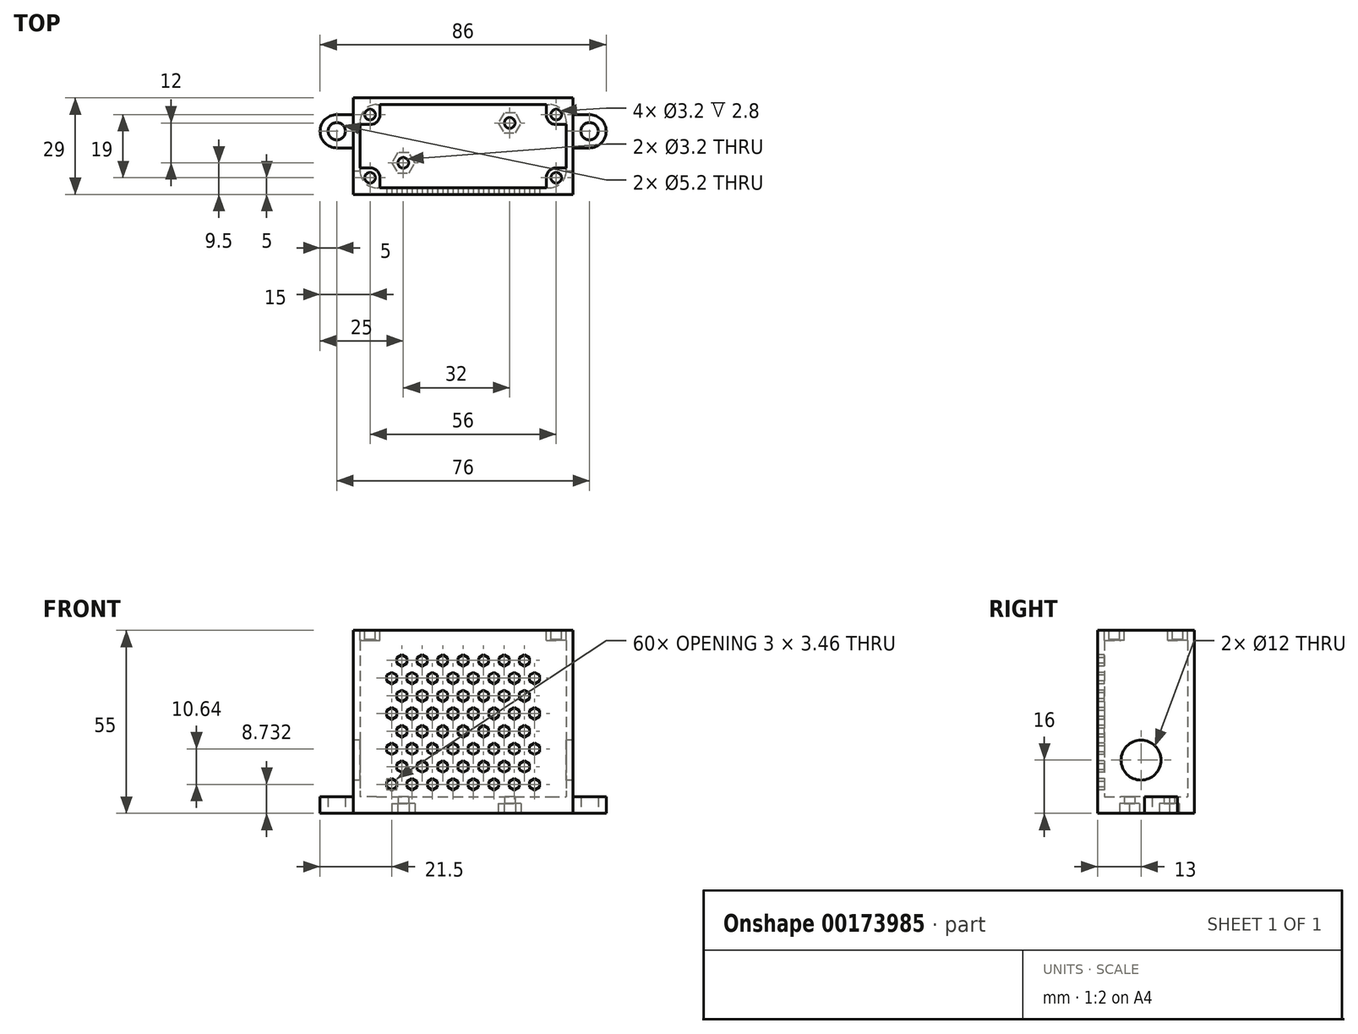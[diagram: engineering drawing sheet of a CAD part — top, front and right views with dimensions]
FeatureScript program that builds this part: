
annotation { "Feature Type Name" : "Feature", "Feature Type Description" : "" }
export const myFeature = defineFeature(function(context is Context, id is Id, definition is map)
    precondition{}
    {
        {
            var Q0;
            Q0=qCreatedBy(makeId("Top.planeOp"),FACE);
            var sketch = newSketch(context, id + "F0", { "sketchPlane" : qUnion([Q0])});
            skCircle(sketch, "E0", {"center": v(3, 5.5) * mm, "radius": 1.6 * mm});
            skCircle(sketch, "E1", {"center": v(35, 17.5) * mm, "radius": 1.6 * mm});
            skLineSegment(sketch, "E2.bottom", {"start": v(0, 0) * mm, "end": v(42, 0) * mm});
            skLineSegment(sketch, "E2.top", {"start": v(0, 21) * mm, "end": v(42, 21) * mm});
            skLineSegment(sketch, "E2.left", {"start": v(0, 0) * mm, "end": v(0, 21) * mm});
            skLineSegment(sketch, "E2.right", {"start": v(42, 0) * mm, "end": v(42, 21) * mm});
            skLineSegment(sketch, "E3.bottom", {"start": v(-12, 25) * mm, "end": v(54, 25) * mm});
            skLineSegment(sketch, "E3.top", {"start": v(-12, -4) * mm, "end": v(54, -4) * mm});
            skLineSegment(sketch, "E3.left", {"start": v(-12, 25) * mm, "end": v(-12, 20) * mm});
            skLineSegment(sketch, "E3.right", {"start": v(54, 25) * mm, "end": v(54, 20) * mm});
            skCircle(sketch, "E4", {"center": v(-17, 15) * mm, "radius": 2.6 * mm});
            skArc(sketch, "E5", {"start": v(-17, 20) * mm, "mid": v(-22, 15) * mm, "end": v(-17, 10) * mm});
            skCircle(sketch, "E6", {"center": v(59, 15) * mm, "radius": 2.6 * mm});
            skArc(sketch, "E7", {"start": v(59, 10) * mm, "mid": v(64, 15) * mm, "end": v(59, 20) * mm});
            skLineSegment(sketch, "E8", {"start": v(-17, 20) * mm, "end": v(-12, 20) * mm});
            skLineSegment(sketch, "E9", {"start": v(-17, 10) * mm, "end": v(-12, 10) * mm});
            skLineSegment(sketch, "E10", {"start": v(59, 20) * mm, "end": v(54, 20) * mm});
            skLineSegment(sketch, "E11", {"start": v(59, 10) * mm, "end": v(54, 10) * mm});
            skLineSegment(sketch, "E12.trimOffspring", {"start": v(54, 10) * mm, "end": v(54, -4) * mm});
            skLineSegment(sketch, "E13.trimOffspring", {"start": v(-12, 10) * mm, "end": v(-12, -4) * mm});
            skSolve(sketch);
        }
        {
            var Q0;
            Q0=makeQuery(id+"F0.imprint","IMPRINT",FACE,{"disambiguationData":[TD([[makeQuery(id+"F0.imprint","IMPRINT",EDGE,{"derivedFrom":sQuery(id+"F0.wireOp",EDGE,"E2.bottom")}),-1.0]])]});
            var Q1;
            Q1=makeQuery(id+"F0.imprint","IMPRINT",FACE,{"disambiguationData":[TD([[makeQuery(id+"F0.imprint","IMPRINT",EDGE,{"derivedFrom":sQuery(id+"F0.wireOp",EDGE,"E0")}),-1.0]])]});
            extrude(context, id + "F1", {"entities" : qUnion([Q0, Q1]), "depth" : 5 * mm});
        }
        {
            var Q0;
            Q0=makeQuery(id+"F1.opExtrude","CAP_FACE",FACE,{"disambiguationData":[OSD([sQuery(id+"F0.wireOp",EDGE,"E0"),sQuery(id+"F0.wireOp",EDGE,"E1"),sQuery(id+"F0.wireOp",EDGE,"E3.bottom"),sQuery(id+"F0.wireOp",EDGE,"E3.top"),sQuery(id+"F0.wireOp",EDGE,"E3.left"),sQuery(id+"F0.wireOp",EDGE,"E3.right"),sQuery(id+"F0.wireOp",EDGE,"E4"),sQuery(id+"F0.wireOp",EDGE,"E5"),sQuery(id+"F0.wireOp",EDGE,"E6"),sQuery(id+"F0.wireOp",EDGE,"E7"),sQuery(id+"F0.wireOp",EDGE,"E8"),sQuery(id+"F0.wireOp",EDGE,"E9"),sQuery(id+"F0.wireOp",EDGE,"E10"),sQuery(id+"F0.wireOp",EDGE,"E11"),sQuery(id+"F0.wireOp",EDGE,"E12.trimOffspring"),sQuery(id+"F0.wireOp",EDGE,"E13.trimOffspring")])],"isStart":false});
            var sketch = newSketch(context, id + "F2", { "sketchPlane" : qUnion([Q0])});
            skLineSegment(sketch, "E14.bottom", {"start": v(-10, 23) * mm, "end": v(52, 23) * mm});
            skLineSegment(sketch, "E14.top", {"start": v(-10, -2) * mm, "end": v(52, -2) * mm});
            skLineSegment(sketch, "E14.left", {"start": v(-10, 23) * mm, "end": v(-10, -2) * mm});
            skLineSegment(sketch, "E14.right", {"start": v(52, 23) * mm, "end": v(52, -2) * mm});
            skLineSegment(sketch, "E15.bottom", {"start": v(-12, 25) * mm, "end": v(54, 25) * mm});
            skLineSegment(sketch, "E15.top", {"start": v(-12, -4) * mm, "end": v(54, -4) * mm});
            skLineSegment(sketch, "E15.left", {"start": v(-12, 25) * mm, "end": v(-12, -4) * mm});
            skLineSegment(sketch, "E15.right", {"start": v(54, 25) * mm, "end": v(54, -4) * mm});
            skSolve(sketch);
        }
        {
            var Q0;
            Q0=makeQuery(id+"F2.imprint","IMPRINT",FACE,{"disambiguationData":[TD([[makeQuery(id+"F2.imprint","IMPRINT",EDGE,{"derivedFrom":sQuery(id+"F2.wireOp",EDGE,"E14.bottom")}),1.0]])]});
            extrude(context, id + "F3", {"entities" : qUnion([Q0]), "operationType" : NewBodyOperationType.ADD, "depth" : 50 * mm});
        }
        {
            var Q0;
            Q0=makeQuery(id+"F1.opExtrude","CAP_FACE",FACE,{"disambiguationData":[OSD([sQuery(id+"F0.wireOp",EDGE,"E0"),sQuery(id+"F0.wireOp",EDGE,"E1"),sQuery(id+"F0.wireOp",EDGE,"E3.bottom"),sQuery(id+"F0.wireOp",EDGE,"E3.top"),sQuery(id+"F0.wireOp",EDGE,"E3.left"),sQuery(id+"F0.wireOp",EDGE,"E3.right"),sQuery(id+"F0.wireOp",EDGE,"E4"),sQuery(id+"F0.wireOp",EDGE,"E5"),sQuery(id+"F0.wireOp",EDGE,"E6"),sQuery(id+"F0.wireOp",EDGE,"E7"),sQuery(id+"F0.wireOp",EDGE,"E8"),sQuery(id+"F0.wireOp",EDGE,"E9"),sQuery(id+"F0.wireOp",EDGE,"E10"),sQuery(id+"F0.wireOp",EDGE,"E11"),sQuery(id+"F0.wireOp",EDGE,"E12.trimOffspring"),sQuery(id+"F0.wireOp",EDGE,"E13.trimOffspring")])],"isStart":true});
            var sketch = newSketch(context, id + "F4", { "sketchPlane" : qUnion([Q0])});
            skCircle(sketch, "E16.cCircle", {"center": v(3, -5.5) * mm, "radius": 3 * mm, "construction": true});
            skLineSegment(sketch, "E16.0", {"start": v(1.27, -2.5) * mm, "end": v(4.73, -2.5) * mm});
            skLineSegment(sketch, "E16.1", {"start": v(4.73, -2.5) * mm, "end": v(6.46, -5.5) * mm});
            skLineSegment(sketch, "E16.2", {"start": v(6.46, -5.5) * mm, "end": v(4.73, -8.5) * mm});
            skLineSegment(sketch, "E16.3", {"start": v(4.73, -8.5) * mm, "end": v(1.27, -8.5) * mm});
            skLineSegment(sketch, "E16.4", {"start": v(1.27, -8.5) * mm, "end": v(-0.46, -5.5) * mm});
            skLineSegment(sketch, "E16.5", {"start": v(-0.46, -5.5) * mm, "end": v(1.27, -2.5) * mm});
            skPoint(sketch, "E16.0.midPoint", {"position": v(3, -2.5) * mm});
            skCircle(sketch, "E17.cCircle", {"center": v(35, -17.5) * mm, "radius": 3 * mm, "construction": true});
            skLineSegment(sketch, "E17.0", {"start": v(33.27, -14.5) * mm, "end": v(36.73, -14.5) * mm});
            skLineSegment(sketch, "E17.1", {"start": v(36.73, -14.5) * mm, "end": v(38.46, -17.5) * mm});
            skLineSegment(sketch, "E17.2", {"start": v(38.46, -17.5) * mm, "end": v(36.73, -20.5) * mm});
            skLineSegment(sketch, "E17.3", {"start": v(36.73, -20.5) * mm, "end": v(33.27, -20.5) * mm});
            skLineSegment(sketch, "E17.4", {"start": v(33.27, -20.5) * mm, "end": v(31.54, -17.5) * mm});
            skLineSegment(sketch, "E17.5", {"start": v(31.54, -17.5) * mm, "end": v(33.27, -14.5) * mm});
            skPoint(sketch, "E17.0.midPoint", {"position": v(35, -14.5) * mm});
            skSolve(sketch);
        }
        {
            var Q0;
            Q0=makeQuery(id+"F4.imprint","IMPRINT",FACE,{"disambiguationData":[TD([[makeQuery(id+"F4.imprint","IMPRINT",EDGE,{"derivedFrom":sQuery(id+"F4.wireOp",EDGE,"E16.0")}),-1.0]])]});
            var Q1;
            Q1=makeQuery(id+"F4.imprint","IMPRINT",FACE,{"disambiguationData":[TD([[makeQuery(id+"F4.imprint","IMPRINT",EDGE,{"derivedFrom":sQuery(id+"F4.wireOp",EDGE,"E17.0")}),-1.0]])]});
            extrude(context, id + "F5", {"entities" : qUnion([Q0, Q1]), "operationType" : NewBodyOperationType.REMOVE, "oppositeDirection" : true, "depth" : 3 * mm});
        }
        {
            var Q0;
            Q0=makeQuery(id+"F3.opExtrude","CAP_FACE",FACE,{"disambiguationData":[OSD([sQuery(id+"F2.wireOp",EDGE,"E14.bottom"),sQuery(id+"F2.wireOp",EDGE,"E14.top"),sQuery(id+"F2.wireOp",EDGE,"E14.left"),sQuery(id+"F2.wireOp",EDGE,"E14.right"),sQuery(id+"F2.wireOp",EDGE,"E15.bottom"),sQuery(id+"F2.wireOp",EDGE,"E15.top"),sQuery(id+"F2.wireOp",EDGE,"E15.left"),sQuery(id+"F2.wireOp",EDGE,"E15.right")])],"isStart":false});
            var sketch = newSketch(context, id + "F6", { "sketchPlane" : qUnion([Q0])});
            skArc(sketch, "E18", {"start": v(-7, 17) * mm, "mid": v(-4.88, 17.88) * mm, "end": v(-4, 20) * mm});
            skArc(sketch, "E19", {"start": v(46, 20) * mm, "mid": v(46.88, 17.88) * mm, "end": v(49, 17) * mm});
            skArc(sketch, "E20", {"start": v(49, 4) * mm, "mid": v(46.88, 3.12) * mm, "end": v(46, 1) * mm});
            skArc(sketch, "E21", {"start": v(-4, 1) * mm, "mid": v(-4.88, 3.12) * mm, "end": v(-7, 4) * mm});
            skLineSegment(sketch, "E22", {"start": v(-10, 23) * mm, "end": v(-10, 20) * mm});
            skLineSegment(sketch, "E23", {"start": v(-10, 23) * mm, "end": v(-7, 23) * mm});
            skLineSegment(sketch, "E24", {"start": v(-10, -2) * mm, "end": v(-10, 1) * mm});
            skLineSegment(sketch, "E25", {"start": v(-7, -2) * mm, "end": v(-10, -2) * mm});
            skLineSegment(sketch, "E26", {"start": v(52, -2) * mm, "end": v(49, -2) * mm});
            skLineSegment(sketch, "E27", {"start": v(52, -2) * mm, "end": v(52, 1) * mm});
            skLineSegment(sketch, "E28", {"start": v(52, 23) * mm, "end": v(49, 23) * mm});
            skLineSegment(sketch, "E29", {"start": v(52, 23) * mm, "end": v(52, 20) * mm});
            skLineSegment(sketch, "E30", {"start": v(46, 23) * mm, "end": v(46, 20) * mm});
            skLineSegment(sketch, "E31", {"start": v(52, 17) * mm, "end": v(49, 17) * mm});
            skLineSegment(sketch, "E32", {"start": v(52, 4) * mm, "end": v(49, 4) * mm});
            skLineSegment(sketch, "E33", {"start": v(46, -2) * mm, "end": v(46, 1) * mm});
            skLineSegment(sketch, "E34", {"start": v(-4, -2) * mm, "end": v(-4, 1) * mm});
            skLineSegment(sketch, "E35", {"start": v(-10, 4) * mm, "end": v(-7, 4) * mm});
            skLineSegment(sketch, "E36", {"start": v(-10, 17) * mm, "end": v(-7, 17) * mm});
            skLineSegment(sketch, "E37", {"start": v(-4, 23) * mm, "end": v(-4, 20) * mm});
            skSolve(sketch);
        }
        {
            var Q0;
            Q0=makeQuery(id+"F6.imprint","IMPRINT",FACE,{"disambiguationData":[TD([[makeQuery(id+"F6.imprint","IMPRINT",EDGE,{"derivedFrom":sQuery(id+"F6.wireOp",EDGE,"E19")}),1.0]])]});
            var Q1;
            Q1=makeQuery(id+"F6.imprint","IMPRINT",FACE,{"disambiguationData":[TD([[makeQuery(id+"F6.imprint","IMPRINT",EDGE,{"derivedFrom":sQuery(id+"F6.wireOp",EDGE,"E20")}),1.0]])]});
            var Q2;
            Q2=makeQuery(id+"F6.imprint","IMPRINT",FACE,{"disambiguationData":[TD([[makeQuery(id+"F6.imprint","IMPRINT",EDGE,{"derivedFrom":sQuery(id+"F6.wireOp",EDGE,"E21")}),1.0]])]});
            var Q3;
            Q3=makeQuery(id+"F6.imprint","IMPRINT",FACE,{"disambiguationData":[TD([[makeQuery(id+"F6.imprint","IMPRINT",EDGE,{"derivedFrom":sQuery(id+"F6.wireOp",EDGE,"E18")}),1.0]])]});
            extrude(context, id + "F7", {"entities" : qUnion([Q0, Q1, Q2, Q3]), "operationType" : NewBodyOperationType.ADD, "oppositeDirection" : true, "depth" : 3 * mm});
        }
        {
            var Q0;
            Q0=makeQuery(id+"F7.opExtrude","CAP_EDGE",EDGE,{"disambiguationData":[OSD([sQuery(id+"F2.wireOp",EDGE,"E14.top"),sQuery(id+"F6.wireOp",EDGE,"E25")])],"isStart":false});
            var Q1;
            Q1=makeQuery(id+"F7.opExtrude","CAP_EDGE",EDGE,{"disambiguationData":[OSD([sQuery(id+"F2.wireOp",EDGE,"E14.left"),sQuery(id+"F6.wireOp",EDGE,"E24")])],"isStart":false});
            var Q2;
            Q2=makeQuery(id+"F3.opExtrude","SWEPT_EDGE",EDGE,{"disambiguationData":[OSD([sQuery(id+"F2.wireOp",EDGE,"E14.top"),sQuery(id+"F2.wireOp",EDGE,"E14.left")])]});
            var Q3;
            Q3=makeQuery(id+"F3.opExtrude","SWEPT_EDGE",EDGE,{"disambiguationData":[OSD([sQuery(id+"F2.wireOp",EDGE,"E14.bottom"),sQuery(id+"F2.wireOp",EDGE,"E14.left")])]});
            var Q4;
            Q4=makeQuery(id+"F3.opExtrude","SWEPT_EDGE",EDGE,{"disambiguationData":[OSD([sQuery(id+"F2.wireOp",EDGE,"E14.bottom"),sQuery(id+"F2.wireOp",EDGE,"E14.right")])]});
            var Q5;
            Q5=makeQuery(id+"F3.opExtrude","SWEPT_EDGE",EDGE,{"disambiguationData":[OSD([sQuery(id+"F2.wireOp",EDGE,"E14.top"),sQuery(id+"F2.wireOp",EDGE,"E14.right")])]});
            var Q6;
            Q6=makeQuery(id+"F7.opExtrude","CAP_EDGE",EDGE,{"disambiguationData":[OSD([sQuery(id+"F2.wireOp",EDGE,"E14.left"),sQuery(id+"F6.wireOp",EDGE,"E22")])],"isStart":false});
            var Q7;
            Q7=makeQuery(id+"F7.opExtrude","CAP_EDGE",EDGE,{"disambiguationData":[OSD([sQuery(id+"F2.wireOp",EDGE,"E14.bottom"),sQuery(id+"F6.wireOp",EDGE,"E23")])],"isStart":false});
            var Q8;
            Q8=makeQuery(id+"F7.opExtrude","CAP_EDGE",EDGE,{"disambiguationData":[OSD([sQuery(id+"F2.wireOp",EDGE,"E14.right"),sQuery(id+"F6.wireOp",EDGE,"E29")])],"isStart":false});
            var Q9;
            Q9=makeQuery(id+"F7.opExtrude","CAP_EDGE",EDGE,{"disambiguationData":[OSD([sQuery(id+"F2.wireOp",EDGE,"E14.bottom"),sQuery(id+"F6.wireOp",EDGE,"E28")])],"isStart":false});
            var Q10;
            Q10=makeQuery(id+"F7.opExtrude","CAP_EDGE",EDGE,{"disambiguationData":[OSD([sQuery(id+"F2.wireOp",EDGE,"E14.top"),sQuery(id+"F6.wireOp",EDGE,"E26")])],"isStart":false});
            var Q11;
            Q11=makeQuery(id+"F7.opExtrude","CAP_EDGE",EDGE,{"disambiguationData":[OSD([sQuery(id+"F2.wireOp",EDGE,"E14.right"),sQuery(id+"F6.wireOp",EDGE,"E27")])],"isStart":false});
            fillet(context, id + "F8", {"entities" : qUnion([Q0, Q1, Q2, Q3, Q4, Q5, Q6, Q7, Q8, Q9, Q10, Q11]), "radius" : 5 * mm, "tangentPropagation" : true, "allowEdgeOverflow" : false});
        }
        {
            var Q0;
            {var subQ0=sQuery(id+"F2.wireOp",EDGE,"E14.left");var subQ1=sQuery(id+"F2.wireOp",EDGE,"E14.top");var subQ2=sQuery(id+"F2.wireOp",EDGE,"E14.right");var subQ3=sQuery(id+"F2.wireOp",EDGE,"E14.bottom");Q0=makeQuery(id+"F7.boolean.opBoolean","MERGE",FACE,{"derivedFrom":[makeQuery(id+"F3.opExtrude","CAP_FACE",FACE,{"disambiguationData":[OSD([subQ3,subQ1,subQ0,subQ2,sQuery(id+"F2.wireOp",EDGE,"E15.bottom"),sQuery(id+"F2.wireOp",EDGE,"E15.top"),sQuery(id+"F2.wireOp",EDGE,"E15.left"),sQuery(id+"F2.wireOp",EDGE,"E15.right")])],"isStart":false}),makeQuery(id+"F7.opExtrude","CAP_FACE",FACE,{"disambiguationData":[OSD([subQ3,subQ0,sQuery(id+"F6.wireOp",EDGE,"E18"),sQuery(id+"F6.wireOp",EDGE,"E22"),sQuery(id+"F6.wireOp",EDGE,"E23"),sQuery(id+"F6.wireOp",EDGE,"E36"),sQuery(id+"F6.wireOp",EDGE,"E37")])],"isStart":true}),makeQuery(id+"F7.opExtrude","CAP_FACE",FACE,{"disambiguationData":[OSD([subQ3,subQ2,sQuery(id+"F6.wireOp",EDGE,"E19"),sQuery(id+"F6.wireOp",EDGE,"E28"),sQuery(id+"F6.wireOp",EDGE,"E29"),sQuery(id+"F6.wireOp",EDGE,"E30"),sQuery(id+"F6.wireOp",EDGE,"E31")])],"isStart":true}),makeQuery(id+"F7.opExtrude","CAP_FACE",FACE,{"disambiguationData":[OSD([subQ1,subQ2,sQuery(id+"F6.wireOp",EDGE,"E20"),sQuery(id+"F6.wireOp",EDGE,"E26"),sQuery(id+"F6.wireOp",EDGE,"E27"),sQuery(id+"F6.wireOp",EDGE,"E32"),sQuery(id+"F6.wireOp",EDGE,"E33")])],"isStart":true}),makeQuery(id+"F7.opExtrude","CAP_FACE",FACE,{"disambiguationData":[OSD([subQ1,subQ0,sQuery(id+"F6.wireOp",EDGE,"E21"),sQuery(id+"F6.wireOp",EDGE,"E24"),sQuery(id+"F6.wireOp",EDGE,"E25"),sQuery(id+"F6.wireOp",EDGE,"E34"),sQuery(id+"F6.wireOp",EDGE,"E35")])],"isStart":true})]});}
            var sketch = newSketch(context, id + "F9", { "sketchPlane" : qUnion([Q0])});
            skCircle(sketch, "E38", {"center": v(-7, 20) * mm, "radius": 1.6 * mm});
            skCircle(sketch, "E39", {"center": v(-7, 1) * mm, "radius": 1.6 * mm});
            skCircle(sketch, "E40", {"center": v(49, 1) * mm, "radius": 1.6 * mm});
            skCircle(sketch, "E41", {"center": v(49, 20) * mm, "radius": 1.6 * mm});
            skSolve(sketch);
        }
        {
            var Q0;
            Q0=makeQuery(id+"F9.imprint","IMPRINT",FACE,{"disambiguationData":[TD([[makeQuery(id+"F9.imprint","IMPRINT",EDGE,{"derivedFrom":sQuery(id+"F9.wireOp",EDGE,"E38")}),1.0]])]});
            var Q1;
            Q1=makeQuery(id+"F9.imprint","IMPRINT",FACE,{"disambiguationData":[TD([[makeQuery(id+"F9.imprint","IMPRINT",EDGE,{"derivedFrom":sQuery(id+"F9.wireOp",EDGE,"E39")}),1.0]])]});
            var Q2;
            Q2=makeQuery(id+"F9.imprint","IMPRINT",FACE,{"disambiguationData":[TD([[makeQuery(id+"F9.imprint","IMPRINT",EDGE,{"derivedFrom":sQuery(id+"F9.wireOp",EDGE,"E40")}),1.0]])]});
            var Q3;
            Q3=makeQuery(id+"F9.imprint","IMPRINT",FACE,{"disambiguationData":[TD([[makeQuery(id+"F9.imprint","IMPRINT",EDGE,{"derivedFrom":sQuery(id+"F9.wireOp",EDGE,"E41")}),1.0]])]});
            extrude(context, id + "F10", {"entities" : qUnion([Q0, Q1, Q2, Q3]), "operationType" : NewBodyOperationType.REMOVE, "oppositeDirection" : true, "depth" : 2.8 * mm});
        }
        {
            var Q0;
            Q0=makeQuery(id+"F3.boolean.opBoolean","MERGE",FACE,{"derivedFrom":[makeQuery(id+"F1.opExtrude","SWEPT_FACE",FACE,{"disambiguationData":[OSD([sQuery(id+"F0.wireOp",EDGE,"E3.left")])]}),makeQuery(id+"F1.opExtrude","SWEPT_FACE",FACE,{"disambiguationData":[OSD([sQuery(id+"F0.wireOp",EDGE,"E13.trimOffspring")])]}),makeQuery(id+"F3.opExtrude","SWEPT_FACE",FACE,{"disambiguationData":[OSD([sQuery(id+"F2.wireOp",EDGE,"E15.left")])]})]});
            var sketch = newSketch(context, id + "F11", { "sketchPlane" : qUnion([Q0])});
            skCircle(sketch, "E42", {"center": v(-9, 16) * mm, "radius": 6 * mm});
            skSolve(sketch);
        }
        {
            var Q0;
            Q0=makeQuery(id+"F11.imprint","IMPRINT",FACE,{"disambiguationData":[TD([[makeQuery(id+"F11.imprint","IMPRINT",EDGE,{"derivedFrom":sQuery(id+"F11.wireOp",EDGE,"E42")}),1.0]])]});
            extrude(context, id + "F12", {"entities" : qUnion([Q0]), "operationType" : NewBodyOperationType.REMOVE, "endBound" : BoundingType.THROUGH_ALL, "oppositeDirection" : true, "depth" : 25 * mm});
        }
        {
            var Q0;
            Q0=makeQuery(id+"F3.boolean.opBoolean","MERGE",FACE,{"derivedFrom":[makeQuery(id+"F1.opExtrude","SWEPT_FACE",FACE,{"disambiguationData":[OSD([sQuery(id+"F0.wireOp",EDGE,"E3.top")])]}),makeQuery(id+"F3.opExtrude","SWEPT_FACE",FACE,{"disambiguationData":[OSD([sQuery(id+"F2.wireOp",EDGE,"E15.top")])]})]});
            var sketch = newSketch(context, id + "F13", { "sketchPlane" : qUnion([Q0])});
            skCircle(sketch, "E43.cCircle", {"center": v(-0.5, 8.73) * mm, "radius": 1.5 * mm, "construction": true});
            skLineSegment(sketch, "E43.0", {"start": v(-0.5, 10.46) * mm, "end": v(1, 9.6) * mm});
            skLineSegment(sketch, "E43.1", {"start": v(1, 9.6) * mm, "end": v(1, 7.87) * mm});
            skLineSegment(sketch, "E43.2", {"start": v(1, 7.87) * mm, "end": v(-0.5, 7) * mm});
            skLineSegment(sketch, "E43.3", {"start": v(-0.5, 7) * mm, "end": v(-2, 7.87) * mm});
            skLineSegment(sketch, "E43.4", {"start": v(-2, 7.87) * mm, "end": v(-2, 9.6) * mm});
            skLineSegment(sketch, "E43.5", {"start": v(-2, 9.6) * mm, "end": v(-0.5, 10.46) * mm});
            skPoint(sketch, "E43.0.midPoint", {"position": v(0.25, 10.03) * mm});
            skCircle(sketch, "E44.1.0.0", {"center": v(5.64, 8.73) * mm, "radius": 1.5 * mm, "construction": true});
            skPoint(sketch, "E44.1.0.1", {"position": v(6.4, 10.03) * mm});
            skLineSegment(sketch, "E44.1.0.2", {"start": v(4.14, 7.87) * mm, "end": v(4.14, 9.6) * mm});
            skLineSegment(sketch, "E44.1.0.3", {"start": v(5.64, 7) * mm, "end": v(4.14, 7.87) * mm});
            skLineSegment(sketch, "E44.1.0.4", {"start": v(7.14, 7.87) * mm, "end": v(5.64, 7) * mm});
            skLineSegment(sketch, "E44.1.0.5", {"start": v(7.14, 9.6) * mm, "end": v(7.14, 7.87) * mm});
            skLineSegment(sketch, "E44.1.0.6", {"start": v(5.64, 10.46) * mm, "end": v(7.14, 9.6) * mm});
            skLineSegment(sketch, "E44.1.0.7", {"start": v(4.14, 9.6) * mm, "end": v(5.64, 10.46) * mm});
            skCircle(sketch, "E44.2.0.0", {"center": v(11.79, 8.73) * mm, "radius": 1.5 * mm, "construction": true});
            skPoint(sketch, "E44.2.0.1", {"position": v(12.54, 10.03) * mm});
            skLineSegment(sketch, "E44.2.0.2", {"start": v(10.29, 7.87) * mm, "end": v(10.29, 9.6) * mm});
            skLineSegment(sketch, "E44.2.0.3", {"start": v(11.79, 7) * mm, "end": v(10.29, 7.87) * mm});
            skLineSegment(sketch, "E44.2.0.4", {"start": v(13.29, 7.87) * mm, "end": v(11.79, 7) * mm});
            skLineSegment(sketch, "E44.2.0.5", {"start": v(13.29, 9.6) * mm, "end": v(13.29, 7.87) * mm});
            skLineSegment(sketch, "E44.2.0.6", {"start": v(11.79, 10.46) * mm, "end": v(13.29, 9.6) * mm});
            skLineSegment(sketch, "E44.2.0.7", {"start": v(10.29, 9.6) * mm, "end": v(11.79, 10.46) * mm});
            skCircle(sketch, "E44.3.0.0", {"center": v(17.93, 8.73) * mm, "radius": 1.5 * mm, "construction": true});
            skPoint(sketch, "E44.3.0.1", {"position": v(18.68, 10.03) * mm});
            skLineSegment(sketch, "E44.3.0.2", {"start": v(16.43, 7.87) * mm, "end": v(16.43, 9.6) * mm});
            skLineSegment(sketch, "E44.3.0.3", {"start": v(17.93, 7) * mm, "end": v(16.43, 7.87) * mm});
            skLineSegment(sketch, "E44.3.0.4", {"start": v(19.43, 7.87) * mm, "end": v(17.93, 7) * mm});
            skLineSegment(sketch, "E44.3.0.5", {"start": v(19.43, 9.6) * mm, "end": v(19.43, 7.87) * mm});
            skLineSegment(sketch, "E44.3.0.6", {"start": v(17.93, 10.46) * mm, "end": v(19.43, 9.6) * mm});
            skLineSegment(sketch, "E44.3.0.7", {"start": v(16.43, 9.6) * mm, "end": v(17.93, 10.46) * mm});
            skCircle(sketch, "E44.4.0.0", {"center": v(24.07, 8.73) * mm, "radius": 1.5 * mm, "construction": true});
            skPoint(sketch, "E44.4.0.1", {"position": v(24.82, 10.03) * mm});
            skLineSegment(sketch, "E44.4.0.2", {"start": v(22.57, 7.87) * mm, "end": v(22.57, 9.6) * mm});
            skLineSegment(sketch, "E44.4.0.3", {"start": v(24.07, 7) * mm, "end": v(22.57, 7.87) * mm});
            skLineSegment(sketch, "E44.4.0.4", {"start": v(25.57, 7.87) * mm, "end": v(24.07, 7) * mm});
            skLineSegment(sketch, "E44.4.0.5", {"start": v(25.57, 9.6) * mm, "end": v(25.57, 7.87) * mm});
            skLineSegment(sketch, "E44.4.0.6", {"start": v(24.07, 10.46) * mm, "end": v(25.57, 9.6) * mm});
            skLineSegment(sketch, "E44.4.0.7", {"start": v(22.57, 9.6) * mm, "end": v(24.07, 10.46) * mm});
            skCircle(sketch, "E44.5.0.0", {"center": v(30.21, 8.73) * mm, "radius": 1.5 * mm, "construction": true});
            skPoint(sketch, "E44.5.0.1", {"position": v(30.96, 10.03) * mm});
            skLineSegment(sketch, "E44.5.0.2", {"start": v(28.71, 7.87) * mm, "end": v(28.71, 9.6) * mm});
            skLineSegment(sketch, "E44.5.0.3", {"start": v(30.21, 7) * mm, "end": v(28.71, 7.87) * mm});
            skLineSegment(sketch, "E44.5.0.4", {"start": v(31.71, 7.87) * mm, "end": v(30.21, 7) * mm});
            skLineSegment(sketch, "E44.5.0.5", {"start": v(31.71, 9.6) * mm, "end": v(31.71, 7.87) * mm});
            skLineSegment(sketch, "E44.5.0.6", {"start": v(30.21, 10.46) * mm, "end": v(31.71, 9.6) * mm});
            skLineSegment(sketch, "E44.5.0.7", {"start": v(28.71, 9.6) * mm, "end": v(30.21, 10.46) * mm});
            skCircle(sketch, "E44.6.0.0", {"center": v(36.36, 8.73) * mm, "radius": 1.5 * mm, "construction": true});
            skPoint(sketch, "E44.6.0.1", {"position": v(37.1, 10.03) * mm});
            skLineSegment(sketch, "E44.6.0.2", {"start": v(34.86, 7.87) * mm, "end": v(34.86, 9.6) * mm});
            skLineSegment(sketch, "E44.6.0.3", {"start": v(36.36, 7) * mm, "end": v(34.86, 7.87) * mm});
            skLineSegment(sketch, "E44.6.0.4", {"start": v(37.86, 7.87) * mm, "end": v(36.36, 7) * mm});
            skLineSegment(sketch, "E44.6.0.5", {"start": v(37.86, 9.6) * mm, "end": v(37.86, 7.87) * mm});
            skLineSegment(sketch, "E44.6.0.6", {"start": v(36.36, 10.46) * mm, "end": v(37.86, 9.6) * mm});
            skLineSegment(sketch, "E44.6.0.7", {"start": v(34.86, 9.6) * mm, "end": v(36.36, 10.46) * mm});
            skCircle(sketch, "E44.7.0.0", {"center": v(42.5, 8.73) * mm, "radius": 1.5 * mm, "construction": true});
            skPoint(sketch, "E44.7.0.1", {"position": v(43.25, 10.03) * mm});
            skLineSegment(sketch, "E44.7.0.2", {"start": v(41, 7.87) * mm, "end": v(41, 9.6) * mm});
            skLineSegment(sketch, "E44.7.0.3", {"start": v(42.5, 7) * mm, "end": v(41, 7.87) * mm});
            skLineSegment(sketch, "E44.7.0.4", {"start": v(44, 7.87) * mm, "end": v(42.5, 7) * mm});
            skLineSegment(sketch, "E44.7.0.5", {"start": v(44, 9.6) * mm, "end": v(44, 7.87) * mm});
            skLineSegment(sketch, "E44.7.0.6", {"start": v(42.5, 10.46) * mm, "end": v(44, 9.6) * mm});
            skLineSegment(sketch, "E44.7.0.7", {"start": v(41, 9.6) * mm, "end": v(42.5, 10.46) * mm});
            skLineSegment(sketch, "E44.direction1", {"start": v(-2, 7.87) * mm, "end": v(4.14, 7.87) * mm, "construction": true});
            skCircle(sketch, "E45.cCircle", {"center": v(2.57, 14.05) * mm, "radius": 1.5 * mm, "construction": true});
            skLineSegment(sketch, "E45.0", {"start": v(2.57, 15.78) * mm, "end": v(4.07, 14.92) * mm});
            skLineSegment(sketch, "E45.1", {"start": v(4.07, 14.92) * mm, "end": v(4.07, 13.19) * mm});
            skLineSegment(sketch, "E45.2", {"start": v(4.07, 13.19) * mm, "end": v(2.57, 12.32) * mm});
            skLineSegment(sketch, "E45.3", {"start": v(2.57, 12.32) * mm, "end": v(1.07, 13.19) * mm});
            skLineSegment(sketch, "E45.4", {"start": v(1.07, 13.19) * mm, "end": v(1.07, 14.92) * mm});
            skLineSegment(sketch, "E45.5", {"start": v(1.07, 14.92) * mm, "end": v(2.57, 15.78) * mm});
            skPoint(sketch, "E45.0.midPoint", {"position": v(3.32, 15.35) * mm});
            skLineSegment(sketch, "E46", {"start": v(1, 9.6) * mm, "end": v(4.14, 9.6) * mm});
            skPoint(sketch, "E47", {"position": v(2.57, 9.6) * mm});
            skCircle(sketch, "E48.1.0.0", {"center": v(8.71, 14.05) * mm, "radius": 1.5 * mm, "construction": true});
            skLineSegment(sketch, "E48.1.0.1", {"start": v(7.21, 13.19) * mm, "end": v(7.21, 14.92) * mm});
            skLineSegment(sketch, "E48.1.0.2", {"start": v(10.21, 13.19) * mm, "end": v(8.71, 12.32) * mm});
            skLineSegment(sketch, "E48.1.0.3", {"start": v(7.21, 14.92) * mm, "end": v(8.71, 15.78) * mm});
            skPoint(sketch, "E48.1.0.4", {"position": v(9.46, 15.35) * mm});
            skLineSegment(sketch, "E48.1.0.5", {"start": v(8.71, 15.78) * mm, "end": v(10.21, 14.92) * mm});
            skLineSegment(sketch, "E48.1.0.6", {"start": v(8.71, 12.32) * mm, "end": v(7.21, 13.19) * mm});
            skLineSegment(sketch, "E48.1.0.7", {"start": v(10.21, 14.92) * mm, "end": v(10.21, 13.19) * mm});
            skCircle(sketch, "E48.2.0.0", {"center": v(14.86, 14.05) * mm, "radius": 1.5 * mm, "construction": true});
            skLineSegment(sketch, "E48.2.0.1", {"start": v(13.36, 13.19) * mm, "end": v(13.36, 14.92) * mm});
            skLineSegment(sketch, "E48.2.0.2", {"start": v(16.36, 13.19) * mm, "end": v(14.86, 12.32) * mm});
            skLineSegment(sketch, "E48.2.0.3", {"start": v(13.36, 14.92) * mm, "end": v(14.86, 15.78) * mm});
            skPoint(sketch, "E48.2.0.4", {"position": v(15.6, 15.35) * mm});
            skLineSegment(sketch, "E48.2.0.5", {"start": v(14.86, 15.78) * mm, "end": v(16.36, 14.92) * mm});
            skLineSegment(sketch, "E48.2.0.6", {"start": v(14.86, 12.32) * mm, "end": v(13.36, 13.19) * mm});
            skLineSegment(sketch, "E48.2.0.7", {"start": v(16.36, 14.92) * mm, "end": v(16.36, 13.19) * mm});
            skCircle(sketch, "E48.3.0.0", {"center": v(21, 14.05) * mm, "radius": 1.5 * mm, "construction": true});
            skLineSegment(sketch, "E48.3.0.1", {"start": v(19.5, 13.19) * mm, "end": v(19.5, 14.92) * mm});
            skLineSegment(sketch, "E48.3.0.2", {"start": v(22.5, 13.19) * mm, "end": v(21, 12.32) * mm});
            skLineSegment(sketch, "E48.3.0.3", {"start": v(19.5, 14.92) * mm, "end": v(21, 15.78) * mm});
            skPoint(sketch, "E48.3.0.4", {"position": v(21.75, 15.35) * mm});
            skLineSegment(sketch, "E48.3.0.5", {"start": v(21, 15.78) * mm, "end": v(22.5, 14.92) * mm});
            skLineSegment(sketch, "E48.3.0.6", {"start": v(21, 12.32) * mm, "end": v(19.5, 13.19) * mm});
            skLineSegment(sketch, "E48.3.0.7", {"start": v(22.5, 14.92) * mm, "end": v(22.5, 13.19) * mm});
            skCircle(sketch, "E48.4.0.0", {"center": v(27.14, 14.05) * mm, "radius": 1.5 * mm, "construction": true});
            skLineSegment(sketch, "E48.4.0.1", {"start": v(25.64, 13.19) * mm, "end": v(25.64, 14.92) * mm});
            skLineSegment(sketch, "E48.4.0.2", {"start": v(28.64, 13.19) * mm, "end": v(27.14, 12.32) * mm});
            skLineSegment(sketch, "E48.4.0.3", {"start": v(25.64, 14.92) * mm, "end": v(27.14, 15.78) * mm});
            skPoint(sketch, "E48.4.0.4", {"position": v(27.9, 15.35) * mm});
            skLineSegment(sketch, "E48.4.0.5", {"start": v(27.14, 15.78) * mm, "end": v(28.64, 14.92) * mm});
            skLineSegment(sketch, "E48.4.0.6", {"start": v(27.14, 12.32) * mm, "end": v(25.64, 13.19) * mm});
            skLineSegment(sketch, "E48.4.0.7", {"start": v(28.64, 14.92) * mm, "end": v(28.64, 13.19) * mm});
            skCircle(sketch, "E48.5.0.0", {"center": v(33.29, 14.05) * mm, "radius": 1.5 * mm, "construction": true});
            skLineSegment(sketch, "E48.5.0.1", {"start": v(31.79, 13.19) * mm, "end": v(31.79, 14.92) * mm});
            skLineSegment(sketch, "E48.5.0.2", {"start": v(34.79, 13.19) * mm, "end": v(33.29, 12.32) * mm});
            skLineSegment(sketch, "E48.5.0.3", {"start": v(31.79, 14.92) * mm, "end": v(33.29, 15.78) * mm});
            skPoint(sketch, "E48.5.0.4", {"position": v(34.04, 15.35) * mm});
            skLineSegment(sketch, "E48.5.0.5", {"start": v(33.29, 15.78) * mm, "end": v(34.79, 14.92) * mm});
            skLineSegment(sketch, "E48.5.0.6", {"start": v(33.29, 12.32) * mm, "end": v(31.79, 13.19) * mm});
            skLineSegment(sketch, "E48.5.0.7", {"start": v(34.79, 14.92) * mm, "end": v(34.79, 13.19) * mm});
            skCircle(sketch, "E48.6.0.0", {"center": v(39.43, 14.05) * mm, "radius": 1.5 * mm, "construction": true});
            skLineSegment(sketch, "E48.6.0.1", {"start": v(37.93, 13.19) * mm, "end": v(37.93, 14.92) * mm});
            skLineSegment(sketch, "E48.6.0.2", {"start": v(40.93, 13.19) * mm, "end": v(39.43, 12.32) * mm});
            skLineSegment(sketch, "E48.6.0.3", {"start": v(37.93, 14.92) * mm, "end": v(39.43, 15.78) * mm});
            skPoint(sketch, "E48.6.0.4", {"position": v(40.18, 15.35) * mm});
            skLineSegment(sketch, "E48.6.0.5", {"start": v(39.43, 15.78) * mm, "end": v(40.93, 14.92) * mm});
            skLineSegment(sketch, "E48.6.0.6", {"start": v(39.43, 12.32) * mm, "end": v(37.93, 13.19) * mm});
            skLineSegment(sketch, "E48.6.0.7", {"start": v(40.93, 14.92) * mm, "end": v(40.93, 13.19) * mm});
            skLineSegment(sketch, "E48.direction1", {"start": v(1.07, 13.19) * mm, "end": v(7.21, 13.19) * mm, "construction": true});
            skLineSegment(sketch, "E49", {"start": v(37.86, 9.6) * mm, "end": v(41, 9.6) * mm});
            skPoint(sketch, "E50", {"position": v(39.43, 9.6) * mm});
            skLineSegment(sketch, "E51.0.1.0", {"start": v(37.86, 20.24) * mm, "end": v(41, 20.24) * mm});
            skCircle(sketch, "E51.0.1.1", {"center": v(-0.5, 19.37) * mm, "radius": 1.5 * mm, "construction": true});
            skCircle(sketch, "E51.0.1.2", {"center": v(24.07, 19.37) * mm, "radius": 1.5 * mm, "construction": true});
            skLineSegment(sketch, "E51.0.1.3", {"start": v(10.29, 18.5) * mm, "end": v(10.29, 20.24) * mm});
            skCircle(sketch, "E51.0.1.4", {"center": v(11.79, 19.37) * mm, "radius": 1.5 * mm, "construction": true});
            skPoint(sketch, "E51.0.1.5", {"position": v(2.57, 20.24) * mm});
            skCircle(sketch, "E51.0.1.6", {"center": v(17.93, 19.37) * mm, "radius": 1.5 * mm, "construction": true});
            skLineSegment(sketch, "E51.0.1.7", {"start": v(30.21, 17.64) * mm, "end": v(28.71, 18.5) * mm});
            skLineSegment(sketch, "E51.0.1.8", {"start": v(1.07, 23.83) * mm, "end": v(7.21, 23.83) * mm, "construction": true});
            skLineSegment(sketch, "E51.0.1.9", {"start": v(13.36, 25.56) * mm, "end": v(14.86, 26.42) * mm});
            skPoint(sketch, "E51.0.1.10", {"position": v(21.75, 26) * mm});
            skPoint(sketch, "E51.0.1.11", {"position": v(43.25, 20.67) * mm});
            skLineSegment(sketch, "E51.0.1.12", {"start": v(7.21, 25.56) * mm, "end": v(8.71, 26.42) * mm});
            skLineSegment(sketch, "E51.0.1.13", {"start": v(2.57, 22.96) * mm, "end": v(1.07, 23.83) * mm});
            skCircle(sketch, "E51.0.1.14", {"center": v(39.43, 24.7) * mm, "radius": 1.5 * mm, "construction": true});
            skLineSegment(sketch, "E51.0.1.15", {"start": v(10.29, 20.24) * mm, "end": v(11.79, 21.1) * mm});
            skLineSegment(sketch, "E51.0.1.16", {"start": v(37.86, 18.5) * mm, "end": v(36.36, 17.64) * mm});
            skLineSegment(sketch, "E51.0.1.17", {"start": v(44, 18.5) * mm, "end": v(42.5, 17.64) * mm});
            skCircle(sketch, "E51.0.1.18", {"center": v(36.36, 19.37) * mm, "radius": 1.5 * mm, "construction": true});
            skPoint(sketch, "E51.0.1.19", {"position": v(18.68, 20.67) * mm});
            skPoint(sketch, "E51.0.1.20", {"position": v(40.18, 26) * mm});
            skLineSegment(sketch, "E51.0.1.21", {"start": v(28.71, 20.24) * mm, "end": v(30.21, 21.1) * mm});
            skCircle(sketch, "E51.0.1.22", {"center": v(2.57, 24.7) * mm, "radius": 1.5 * mm, "construction": true});
            skLineSegment(sketch, "E51.0.1.23", {"start": v(13.36, 23.83) * mm, "end": v(13.36, 25.56) * mm});
            skPoint(sketch, "E51.0.1.24", {"position": v(15.6, 26) * mm});
            skPoint(sketch, "E51.0.1.25", {"position": v(37.1, 20.67) * mm});
            skLineSegment(sketch, "E51.0.1.26", {"start": v(13.29, 20.24) * mm, "end": v(13.29, 18.5) * mm});
            skLineSegment(sketch, "E51.0.1.27", {"start": v(41, 18.5) * mm, "end": v(41, 20.24) * mm});
            skLineSegment(sketch, "E51.0.1.28", {"start": v(1, 18.5) * mm, "end": v(-0.5, 17.64) * mm});
            skLineSegment(sketch, "E51.0.1.29", {"start": v(36.36, 17.64) * mm, "end": v(34.86, 18.5) * mm});
            skLineSegment(sketch, "E51.0.1.30", {"start": v(4.07, 23.83) * mm, "end": v(2.57, 22.96) * mm});
            skPoint(sketch, "E51.0.1.31", {"position": v(24.82, 20.67) * mm});
            skLineSegment(sketch, "E51.0.1.32", {"start": v(16.36, 25.56) * mm, "end": v(16.36, 23.83) * mm});
            skLineSegment(sketch, "E51.0.1.33", {"start": v(22.5, 25.56) * mm, "end": v(22.5, 23.83) * mm});
            skLineSegment(sketch, "E51.0.1.34", {"start": v(37.93, 23.83) * mm, "end": v(37.93, 25.56) * mm});
            skLineSegment(sketch, "E51.0.1.35", {"start": v(44, 20.24) * mm, "end": v(44, 18.5) * mm});
            skPoint(sketch, "E51.0.1.36", {"position": v(0.25, 20.67) * mm});
            skPoint(sketch, "E51.0.1.37", {"position": v(3.32, 26) * mm});
            skPoint(sketch, "E51.0.1.38", {"position": v(39.43, 20.24) * mm});
            skLineSegment(sketch, "E51.0.1.39", {"start": v(14.86, 22.96) * mm, "end": v(13.36, 23.83) * mm});
            skCircle(sketch, "E51.0.1.40", {"center": v(33.29, 24.7) * mm, "radius": 1.5 * mm, "construction": true});
            skLineSegment(sketch, "E51.0.1.41", {"start": v(10.21, 23.83) * mm, "end": v(8.71, 22.96) * mm});
            skCircle(sketch, "E51.0.1.42", {"center": v(30.21, 19.37) * mm, "radius": 1.5 * mm, "construction": true});
            skLineSegment(sketch, "E51.0.1.43", {"start": v(42.5, 17.64) * mm, "end": v(41, 18.5) * mm});
            skLineSegment(sketch, "E51.0.1.44", {"start": v(25.64, 25.56) * mm, "end": v(27.14, 26.42) * mm});
            skLineSegment(sketch, "E51.0.1.45", {"start": v(19.43, 20.24) * mm, "end": v(19.43, 18.5) * mm});
            skLineSegment(sketch, "E51.0.1.46", {"start": v(-2, 18.5) * mm, "end": v(4.14, 18.5) * mm, "construction": true});
            skCircle(sketch, "E51.0.1.47", {"center": v(14.86, 24.7) * mm, "radius": 1.5 * mm, "construction": true});
            skLineSegment(sketch, "E51.0.1.48", {"start": v(19.43, 18.5) * mm, "end": v(17.93, 17.64) * mm});
            skLineSegment(sketch, "E51.0.1.49", {"start": v(-0.5, 17.64) * mm, "end": v(-2, 18.5) * mm});
            skLineSegment(sketch, "E51.0.1.50", {"start": v(-2, 20.24) * mm, "end": v(-0.5, 21.1) * mm});
            skLineSegment(sketch, "E51.0.1.51", {"start": v(31.71, 18.5) * mm, "end": v(30.21, 17.64) * mm});
            skLineSegment(sketch, "E51.0.1.52", {"start": v(25.57, 18.5) * mm, "end": v(24.07, 17.64) * mm});
            skLineSegment(sketch, "E51.0.1.53", {"start": v(16.43, 18.5) * mm, "end": v(16.43, 20.24) * mm});
            skLineSegment(sketch, "E51.0.1.54", {"start": v(40.93, 23.83) * mm, "end": v(39.43, 22.96) * mm});
            skCircle(sketch, "E51.0.1.55", {"center": v(27.14, 24.7) * mm, "radius": 1.5 * mm, "construction": true});
            skCircle(sketch, "E51.0.1.56", {"center": v(21, 24.7) * mm, "radius": 1.5 * mm, "construction": true});
            skLineSegment(sketch, "E51.0.1.57", {"start": v(8.71, 22.96) * mm, "end": v(7.21, 23.83) * mm});
            skLineSegment(sketch, "E51.0.1.58", {"start": v(1.07, 25.56) * mm, "end": v(2.57, 26.42) * mm});
            skCircle(sketch, "E51.0.1.59", {"center": v(5.64, 19.37) * mm, "radius": 1.5 * mm, "construction": true});
            skLineSegment(sketch, "E51.0.1.60", {"start": v(5.64, 17.64) * mm, "end": v(4.14, 18.5) * mm});
            skLineSegment(sketch, "E51.0.1.61", {"start": v(7.14, 18.5) * mm, "end": v(5.64, 17.64) * mm});
            skPoint(sketch, "E51.0.1.62", {"position": v(27.9, 26) * mm});
            skPoint(sketch, "E51.0.1.63", {"position": v(6.4, 20.67) * mm});
            skPoint(sketch, "E51.0.1.64", {"position": v(9.46, 26) * mm});
            skLineSegment(sketch, "E51.0.1.65", {"start": v(11.79, 17.64) * mm, "end": v(10.29, 18.5) * mm});
            skLineSegment(sketch, "E51.0.1.66", {"start": v(31.79, 25.56) * mm, "end": v(33.29, 26.42) * mm});
            skLineSegment(sketch, "E51.0.1.67", {"start": v(19.5, 23.83) * mm, "end": v(19.5, 25.56) * mm});
            skLineSegment(sketch, "E51.0.1.68", {"start": v(1, 20.24) * mm, "end": v(4.14, 20.24) * mm});
            skPoint(sketch, "E51.0.1.69", {"position": v(30.96, 20.67) * mm});
            skLineSegment(sketch, "E51.0.1.70", {"start": v(17.93, 17.64) * mm, "end": v(16.43, 18.5) * mm});
            skLineSegment(sketch, "E51.0.1.71", {"start": v(41, 20.24) * mm, "end": v(42.5, 21.1) * mm});
            skLineSegment(sketch, "E51.0.1.72", {"start": v(37.93, 25.56) * mm, "end": v(39.43, 26.42) * mm});
            skPoint(sketch, "E51.0.1.73", {"position": v(12.54, 20.67) * mm});
            skCircle(sketch, "E51.0.1.74", {"center": v(42.5, 19.37) * mm, "radius": 1.5 * mm, "construction": true});
            skLineSegment(sketch, "E51.0.1.75", {"start": v(22.5, 23.83) * mm, "end": v(21, 22.96) * mm});
            skCircle(sketch, "E51.0.1.76", {"center": v(8.71, 24.7) * mm, "radius": 1.5 * mm, "construction": true});
            skPoint(sketch, "E51.0.1.77", {"position": v(34.04, 26) * mm});
            skLineSegment(sketch, "E51.0.1.78", {"start": v(4.14, 20.24) * mm, "end": v(5.64, 21.1) * mm});
            skLineSegment(sketch, "E51.0.1.79", {"start": v(21, 22.96) * mm, "end": v(19.5, 23.83) * mm});
            skLineSegment(sketch, "E51.0.1.80", {"start": v(22.57, 18.5) * mm, "end": v(22.57, 20.24) * mm});
            skLineSegment(sketch, "E51.0.1.81", {"start": v(28.71, 18.5) * mm, "end": v(28.71, 20.24) * mm});
            skLineSegment(sketch, "E51.0.1.82", {"start": v(16.36, 23.83) * mm, "end": v(14.86, 22.96) * mm});
            skLineSegment(sketch, "E51.0.1.83", {"start": v(27.14, 26.42) * mm, "end": v(28.64, 25.56) * mm});
            skLineSegment(sketch, "E51.0.1.84", {"start": v(21, 26.42) * mm, "end": v(22.5, 25.56) * mm});
            skLineSegment(sketch, "E51.0.1.85", {"start": v(11.79, 21.1) * mm, "end": v(13.29, 20.24) * mm});
            skLineSegment(sketch, "E51.0.1.86", {"start": v(7.21, 23.83) * mm, "end": v(7.21, 25.56) * mm});
            skLineSegment(sketch, "E51.0.1.87", {"start": v(19.5, 25.56) * mm, "end": v(21, 26.42) * mm});
            skLineSegment(sketch, "E51.0.1.88", {"start": v(33.29, 22.96) * mm, "end": v(31.79, 23.83) * mm});
            skLineSegment(sketch, "E51.0.1.89", {"start": v(1, 20.24) * mm, "end": v(1, 18.5) * mm});
            skLineSegment(sketch, "E51.0.1.90", {"start": v(-0.5, 21.1) * mm, "end": v(1, 20.24) * mm});
            skLineSegment(sketch, "E51.0.1.91", {"start": v(14.86, 26.42) * mm, "end": v(16.36, 25.56) * mm});
            skLineSegment(sketch, "E51.0.1.92", {"start": v(28.64, 25.56) * mm, "end": v(28.64, 23.83) * mm});
            skLineSegment(sketch, "E51.0.1.93", {"start": v(1.07, 23.83) * mm, "end": v(1.07, 25.56) * mm});
            skLineSegment(sketch, "E51.0.1.94", {"start": v(8.71, 26.42) * mm, "end": v(10.21, 25.56) * mm});
            skLineSegment(sketch, "E51.0.1.95", {"start": v(31.79, 23.83) * mm, "end": v(31.79, 25.56) * mm});
            skLineSegment(sketch, "E51.0.1.96", {"start": v(24.07, 17.64) * mm, "end": v(22.57, 18.5) * mm});
            skLineSegment(sketch, "E51.0.1.97", {"start": v(37.86, 20.24) * mm, "end": v(37.86, 18.5) * mm});
            skLineSegment(sketch, "E51.0.1.98", {"start": v(34.86, 18.5) * mm, "end": v(34.86, 20.24) * mm});
            skLineSegment(sketch, "E51.0.1.99", {"start": v(4.07, 25.56) * mm, "end": v(4.07, 23.83) * mm});
            skLineSegment(sketch, "E51.0.1.100", {"start": v(27.14, 22.96) * mm, "end": v(25.64, 23.83) * mm});
            skLineSegment(sketch, "E51.0.1.101", {"start": v(16.43, 20.24) * mm, "end": v(17.93, 21.1) * mm});
            skLineSegment(sketch, "E51.0.1.102", {"start": v(40.93, 25.56) * mm, "end": v(40.93, 23.83) * mm});
            skLineSegment(sketch, "E51.0.1.103", {"start": v(2.57, 26.42) * mm, "end": v(4.07, 25.56) * mm});
            skLineSegment(sketch, "E51.0.1.104", {"start": v(17.93, 21.1) * mm, "end": v(19.43, 20.24) * mm});
            skLineSegment(sketch, "E51.0.1.105", {"start": v(34.79, 25.56) * mm, "end": v(34.79, 23.83) * mm});
            skLineSegment(sketch, "E51.0.1.106", {"start": v(39.43, 22.96) * mm, "end": v(37.93, 23.83) * mm});
            skLineSegment(sketch, "E51.0.1.107", {"start": v(22.57, 20.24) * mm, "end": v(24.07, 21.1) * mm});
            skLineSegment(sketch, "E51.0.1.108", {"start": v(39.43, 26.42) * mm, "end": v(40.93, 25.56) * mm});
            skLineSegment(sketch, "E51.0.1.109", {"start": v(30.21, 21.1) * mm, "end": v(31.71, 20.24) * mm});
            skLineSegment(sketch, "E51.0.1.110", {"start": v(28.64, 23.83) * mm, "end": v(27.14, 22.96) * mm});
            skLineSegment(sketch, "E51.0.1.111", {"start": v(-2, 18.5) * mm, "end": v(-2, 20.24) * mm});
            skLineSegment(sketch, "E51.0.1.112", {"start": v(42.5, 21.1) * mm, "end": v(44, 20.24) * mm});
            skLineSegment(sketch, "E51.0.1.113", {"start": v(36.36, 21.1) * mm, "end": v(37.86, 20.24) * mm});
            skLineSegment(sketch, "E51.0.1.114", {"start": v(34.79, 23.83) * mm, "end": v(33.29, 22.96) * mm});
            skLineSegment(sketch, "E51.0.1.115", {"start": v(4.14, 18.5) * mm, "end": v(4.14, 20.24) * mm});
            skLineSegment(sketch, "E51.0.1.116", {"start": v(7.14, 20.24) * mm, "end": v(7.14, 18.5) * mm});
            skLineSegment(sketch, "E51.0.1.117", {"start": v(5.64, 21.1) * mm, "end": v(7.14, 20.24) * mm});
            skLineSegment(sketch, "E51.0.1.118", {"start": v(34.86, 20.24) * mm, "end": v(36.36, 21.1) * mm});
            skLineSegment(sketch, "E51.0.1.119", {"start": v(25.57, 20.24) * mm, "end": v(25.57, 18.5) * mm});
            skLineSegment(sketch, "E51.0.1.120", {"start": v(25.64, 23.83) * mm, "end": v(25.64, 25.56) * mm});
            skLineSegment(sketch, "E51.0.1.121", {"start": v(10.21, 25.56) * mm, "end": v(10.21, 23.83) * mm});
            skLineSegment(sketch, "E51.0.1.122", {"start": v(31.71, 20.24) * mm, "end": v(31.71, 18.5) * mm});
            skLineSegment(sketch, "E51.0.1.123", {"start": v(24.07, 21.1) * mm, "end": v(25.57, 20.24) * mm});
            skLineSegment(sketch, "E51.0.1.124", {"start": v(13.29, 18.5) * mm, "end": v(11.79, 17.64) * mm});
            skLineSegment(sketch, "E51.0.1.125", {"start": v(33.29, 26.42) * mm, "end": v(34.79, 25.56) * mm});
            skLineSegment(sketch, "E51.0.2.0", {"start": v(37.86, 30.88) * mm, "end": v(41, 30.88) * mm});
            skCircle(sketch, "E51.0.2.1", {"center": v(-0.5, 30.01) * mm, "radius": 1.5 * mm, "construction": true});
            skCircle(sketch, "E51.0.2.2", {"center": v(24.07, 30.01) * mm, "radius": 1.5 * mm, "construction": true});
            skLineSegment(sketch, "E51.0.2.3", {"start": v(10.29, 29.15) * mm, "end": v(10.29, 30.88) * mm});
            skCircle(sketch, "E51.0.2.4", {"center": v(11.79, 30.01) * mm, "radius": 1.5 * mm, "construction": true});
            skPoint(sketch, "E51.0.2.5", {"position": v(2.57, 30.88) * mm});
            skCircle(sketch, "E51.0.2.6", {"center": v(17.93, 30.01) * mm, "radius": 1.5 * mm, "construction": true});
            skLineSegment(sketch, "E51.0.2.7", {"start": v(30.21, 28.28) * mm, "end": v(28.71, 29.15) * mm});
            skLineSegment(sketch, "E51.0.2.8", {"start": v(1.07, 34.47) * mm, "end": v(7.21, 34.47) * mm, "construction": true});
            skLineSegment(sketch, "E51.0.2.9", {"start": v(13.36, 36.2) * mm, "end": v(14.86, 37.06) * mm});
            skPoint(sketch, "E51.0.2.10", {"position": v(21.75, 36.63) * mm});
            skPoint(sketch, "E51.0.2.11", {"position": v(43.25, 31.31) * mm});
            skLineSegment(sketch, "E51.0.2.12", {"start": v(7.21, 36.2) * mm, "end": v(8.71, 37.06) * mm});
            skLineSegment(sketch, "E51.0.2.13", {"start": v(2.57, 33.6) * mm, "end": v(1.07, 34.47) * mm});
            skCircle(sketch, "E51.0.2.14", {"center": v(39.43, 35.33) * mm, "radius": 1.5 * mm, "construction": true});
            skLineSegment(sketch, "E51.0.2.15", {"start": v(10.29, 30.88) * mm, "end": v(11.79, 31.74) * mm});
            skLineSegment(sketch, "E51.0.2.16", {"start": v(37.86, 29.15) * mm, "end": v(36.36, 28.28) * mm});
            skLineSegment(sketch, "E51.0.2.17", {"start": v(44, 29.15) * mm, "end": v(42.5, 28.28) * mm});
            skCircle(sketch, "E51.0.2.18", {"center": v(36.36, 30.01) * mm, "radius": 1.5 * mm, "construction": true});
            skPoint(sketch, "E51.0.2.19", {"position": v(18.68, 31.31) * mm});
            skPoint(sketch, "E51.0.2.20", {"position": v(40.18, 36.63) * mm});
            skLineSegment(sketch, "E51.0.2.21", {"start": v(28.71, 30.88) * mm, "end": v(30.21, 31.74) * mm});
            skCircle(sketch, "E51.0.2.22", {"center": v(2.57, 35.33) * mm, "radius": 1.5 * mm, "construction": true});
            skLineSegment(sketch, "E51.0.2.23", {"start": v(13.36, 34.47) * mm, "end": v(13.36, 36.2) * mm});
            skPoint(sketch, "E51.0.2.24", {"position": v(15.6, 36.63) * mm});
            skPoint(sketch, "E51.0.2.25", {"position": v(37.1, 31.31) * mm});
            skLineSegment(sketch, "E51.0.2.26", {"start": v(13.29, 30.88) * mm, "end": v(13.29, 29.15) * mm});
            skLineSegment(sketch, "E51.0.2.27", {"start": v(41, 29.15) * mm, "end": v(41, 30.88) * mm});
            skLineSegment(sketch, "E51.0.2.28", {"start": v(1, 29.15) * mm, "end": v(-0.5, 28.28) * mm});
            skLineSegment(sketch, "E51.0.2.29", {"start": v(36.36, 28.28) * mm, "end": v(34.86, 29.15) * mm});
            skLineSegment(sketch, "E51.0.2.30", {"start": v(4.07, 34.47) * mm, "end": v(2.57, 33.6) * mm});
            skPoint(sketch, "E51.0.2.31", {"position": v(24.82, 31.31) * mm});
            skLineSegment(sketch, "E51.0.2.32", {"start": v(16.36, 36.2) * mm, "end": v(16.36, 34.47) * mm});
            skLineSegment(sketch, "E51.0.2.33", {"start": v(22.5, 36.2) * mm, "end": v(22.5, 34.47) * mm});
            skLineSegment(sketch, "E51.0.2.34", {"start": v(37.93, 34.47) * mm, "end": v(37.93, 36.2) * mm});
            skLineSegment(sketch, "E51.0.2.35", {"start": v(44, 30.88) * mm, "end": v(44, 29.15) * mm});
            skPoint(sketch, "E51.0.2.36", {"position": v(0.25, 31.31) * mm});
            skPoint(sketch, "E51.0.2.37", {"position": v(3.32, 36.63) * mm});
            skPoint(sketch, "E51.0.2.38", {"position": v(39.43, 30.88) * mm});
            skLineSegment(sketch, "E51.0.2.39", {"start": v(14.86, 33.6) * mm, "end": v(13.36, 34.47) * mm});
            skCircle(sketch, "E51.0.2.40", {"center": v(33.29, 35.33) * mm, "radius": 1.5 * mm, "construction": true});
            skLineSegment(sketch, "E51.0.2.41", {"start": v(10.21, 34.47) * mm, "end": v(8.71, 33.6) * mm});
            skCircle(sketch, "E51.0.2.42", {"center": v(30.21, 30.01) * mm, "radius": 1.5 * mm, "construction": true});
            skLineSegment(sketch, "E51.0.2.43", {"start": v(42.5, 28.28) * mm, "end": v(41, 29.15) * mm});
            skLineSegment(sketch, "E51.0.2.44", {"start": v(25.64, 36.2) * mm, "end": v(27.14, 37.06) * mm});
            skLineSegment(sketch, "E51.0.2.45", {"start": v(19.43, 30.88) * mm, "end": v(19.43, 29.15) * mm});
            skLineSegment(sketch, "E51.0.2.46", {"start": v(-2, 29.15) * mm, "end": v(4.14, 29.15) * mm, "construction": true});
            skCircle(sketch, "E51.0.2.47", {"center": v(14.86, 35.33) * mm, "radius": 1.5 * mm, "construction": true});
            skLineSegment(sketch, "E51.0.2.48", {"start": v(19.43, 29.15) * mm, "end": v(17.93, 28.28) * mm});
            skLineSegment(sketch, "E51.0.2.49", {"start": v(-0.5, 28.28) * mm, "end": v(-2, 29.15) * mm});
            skLineSegment(sketch, "E51.0.2.50", {"start": v(-2, 30.88) * mm, "end": v(-0.5, 31.74) * mm});
            skLineSegment(sketch, "E51.0.2.51", {"start": v(31.71, 29.15) * mm, "end": v(30.21, 28.28) * mm});
            skLineSegment(sketch, "E51.0.2.52", {"start": v(25.57, 29.15) * mm, "end": v(24.07, 28.28) * mm});
            skLineSegment(sketch, "E51.0.2.53", {"start": v(16.43, 29.15) * mm, "end": v(16.43, 30.88) * mm});
            skLineSegment(sketch, "E51.0.2.54", {"start": v(40.93, 34.47) * mm, "end": v(39.43, 33.6) * mm});
            skCircle(sketch, "E51.0.2.55", {"center": v(27.14, 35.33) * mm, "radius": 1.5 * mm, "construction": true});
            skCircle(sketch, "E51.0.2.56", {"center": v(21, 35.33) * mm, "radius": 1.5 * mm, "construction": true});
            skLineSegment(sketch, "E51.0.2.57", {"start": v(8.71, 33.6) * mm, "end": v(7.21, 34.47) * mm});
            skLineSegment(sketch, "E51.0.2.58", {"start": v(1.07, 36.2) * mm, "end": v(2.57, 37.06) * mm});
            skCircle(sketch, "E51.0.2.59", {"center": v(5.64, 30.01) * mm, "radius": 1.5 * mm, "construction": true});
            skLineSegment(sketch, "E51.0.2.60", {"start": v(5.64, 28.28) * mm, "end": v(4.14, 29.15) * mm});
            skLineSegment(sketch, "E51.0.2.61", {"start": v(7.14, 29.15) * mm, "end": v(5.64, 28.28) * mm});
            skPoint(sketch, "E51.0.2.62", {"position": v(27.9, 36.63) * mm});
            skPoint(sketch, "E51.0.2.63", {"position": v(6.4, 31.31) * mm});
            skPoint(sketch, "E51.0.2.64", {"position": v(9.46, 36.63) * mm});
            skLineSegment(sketch, "E51.0.2.65", {"start": v(11.79, 28.28) * mm, "end": v(10.29, 29.15) * mm});
            skLineSegment(sketch, "E51.0.2.66", {"start": v(31.79, 36.2) * mm, "end": v(33.29, 37.06) * mm});
            skLineSegment(sketch, "E51.0.2.67", {"start": v(19.5, 34.47) * mm, "end": v(19.5, 36.2) * mm});
            skLineSegment(sketch, "E51.0.2.68", {"start": v(1, 30.88) * mm, "end": v(4.14, 30.88) * mm});
            skPoint(sketch, "E51.0.2.69", {"position": v(30.96, 31.31) * mm});
            skLineSegment(sketch, "E51.0.2.70", {"start": v(17.93, 28.28) * mm, "end": v(16.43, 29.15) * mm});
            skLineSegment(sketch, "E51.0.2.71", {"start": v(41, 30.88) * mm, "end": v(42.5, 31.74) * mm});
            skLineSegment(sketch, "E51.0.2.72", {"start": v(37.93, 36.2) * mm, "end": v(39.43, 37.06) * mm});
            skPoint(sketch, "E51.0.2.73", {"position": v(12.54, 31.31) * mm});
            skCircle(sketch, "E51.0.2.74", {"center": v(42.5, 30.01) * mm, "radius": 1.5 * mm, "construction": true});
            skLineSegment(sketch, "E51.0.2.75", {"start": v(22.5, 34.47) * mm, "end": v(21, 33.6) * mm});
            skCircle(sketch, "E51.0.2.76", {"center": v(8.71, 35.33) * mm, "radius": 1.5 * mm, "construction": true});
            skPoint(sketch, "E51.0.2.77", {"position": v(34.04, 36.63) * mm});
            skLineSegment(sketch, "E51.0.2.78", {"start": v(4.14, 30.88) * mm, "end": v(5.64, 31.74) * mm});
            skLineSegment(sketch, "E51.0.2.79", {"start": v(21, 33.6) * mm, "end": v(19.5, 34.47) * mm});
            skLineSegment(sketch, "E51.0.2.80", {"start": v(22.57, 29.15) * mm, "end": v(22.57, 30.88) * mm});
            skLineSegment(sketch, "E51.0.2.81", {"start": v(28.71, 29.15) * mm, "end": v(28.71, 30.88) * mm});
            skLineSegment(sketch, "E51.0.2.82", {"start": v(16.36, 34.47) * mm, "end": v(14.86, 33.6) * mm});
            skLineSegment(sketch, "E51.0.2.83", {"start": v(27.14, 37.06) * mm, "end": v(28.64, 36.2) * mm});
            skLineSegment(sketch, "E51.0.2.84", {"start": v(21, 37.06) * mm, "end": v(22.5, 36.2) * mm});
            skLineSegment(sketch, "E51.0.2.85", {"start": v(11.79, 31.74) * mm, "end": v(13.29, 30.88) * mm});
            skLineSegment(sketch, "E51.0.2.86", {"start": v(7.21, 34.47) * mm, "end": v(7.21, 36.2) * mm});
            skLineSegment(sketch, "E51.0.2.87", {"start": v(19.5, 36.2) * mm, "end": v(21, 37.06) * mm});
            skLineSegment(sketch, "E51.0.2.88", {"start": v(33.29, 33.6) * mm, "end": v(31.79, 34.47) * mm});
            skLineSegment(sketch, "E51.0.2.89", {"start": v(1, 30.88) * mm, "end": v(1, 29.15) * mm});
            skLineSegment(sketch, "E51.0.2.90", {"start": v(-0.5, 31.74) * mm, "end": v(1, 30.88) * mm});
            skLineSegment(sketch, "E51.0.2.91", {"start": v(14.86, 37.06) * mm, "end": v(16.36, 36.2) * mm});
            skLineSegment(sketch, "E51.0.2.92", {"start": v(28.64, 36.2) * mm, "end": v(28.64, 34.47) * mm});
            skLineSegment(sketch, "E51.0.2.93", {"start": v(1.07, 34.47) * mm, "end": v(1.07, 36.2) * mm});
            skLineSegment(sketch, "E51.0.2.94", {"start": v(8.71, 37.06) * mm, "end": v(10.21, 36.2) * mm});
            skLineSegment(sketch, "E51.0.2.95", {"start": v(31.79, 34.47) * mm, "end": v(31.79, 36.2) * mm});
            skLineSegment(sketch, "E51.0.2.96", {"start": v(24.07, 28.28) * mm, "end": v(22.57, 29.15) * mm});
            skLineSegment(sketch, "E51.0.2.97", {"start": v(37.86, 30.88) * mm, "end": v(37.86, 29.15) * mm});
            skLineSegment(sketch, "E51.0.2.98", {"start": v(34.86, 29.15) * mm, "end": v(34.86, 30.88) * mm});
            skLineSegment(sketch, "E51.0.2.99", {"start": v(4.07, 36.2) * mm, "end": v(4.07, 34.47) * mm});
            skLineSegment(sketch, "E51.0.2.100", {"start": v(27.14, 33.6) * mm, "end": v(25.64, 34.47) * mm});
            skLineSegment(sketch, "E51.0.2.101", {"start": v(16.43, 30.88) * mm, "end": v(17.93, 31.74) * mm});
            skLineSegment(sketch, "E51.0.2.102", {"start": v(40.93, 36.2) * mm, "end": v(40.93, 34.47) * mm});
            skLineSegment(sketch, "E51.0.2.103", {"start": v(2.57, 37.06) * mm, "end": v(4.07, 36.2) * mm});
            skLineSegment(sketch, "E51.0.2.104", {"start": v(17.93, 31.74) * mm, "end": v(19.43, 30.88) * mm});
            skLineSegment(sketch, "E51.0.2.105", {"start": v(34.79, 36.2) * mm, "end": v(34.79, 34.47) * mm});
            skLineSegment(sketch, "E51.0.2.106", {"start": v(39.43, 33.6) * mm, "end": v(37.93, 34.47) * mm});
            skLineSegment(sketch, "E51.0.2.107", {"start": v(22.57, 30.88) * mm, "end": v(24.07, 31.74) * mm});
            skLineSegment(sketch, "E51.0.2.108", {"start": v(39.43, 37.06) * mm, "end": v(40.93, 36.2) * mm});
            skLineSegment(sketch, "E51.0.2.109", {"start": v(30.21, 31.74) * mm, "end": v(31.71, 30.88) * mm});
            skLineSegment(sketch, "E51.0.2.110", {"start": v(28.64, 34.47) * mm, "end": v(27.14, 33.6) * mm});
            skLineSegment(sketch, "E51.0.2.111", {"start": v(-2, 29.15) * mm, "end": v(-2, 30.88) * mm});
            skLineSegment(sketch, "E51.0.2.112", {"start": v(42.5, 31.74) * mm, "end": v(44, 30.88) * mm});
            skLineSegment(sketch, "E51.0.2.113", {"start": v(36.36, 31.74) * mm, "end": v(37.86, 30.88) * mm});
            skLineSegment(sketch, "E51.0.2.114", {"start": v(34.79, 34.47) * mm, "end": v(33.29, 33.6) * mm});
            skLineSegment(sketch, "E51.0.2.115", {"start": v(4.14, 29.15) * mm, "end": v(4.14, 30.88) * mm});
            skLineSegment(sketch, "E51.0.2.116", {"start": v(7.14, 30.88) * mm, "end": v(7.14, 29.15) * mm});
            skLineSegment(sketch, "E51.0.2.117", {"start": v(5.64, 31.74) * mm, "end": v(7.14, 30.88) * mm});
            skLineSegment(sketch, "E51.0.2.118", {"start": v(34.86, 30.88) * mm, "end": v(36.36, 31.74) * mm});
            skLineSegment(sketch, "E51.0.2.119", {"start": v(25.57, 30.88) * mm, "end": v(25.57, 29.15) * mm});
            skLineSegment(sketch, "E51.0.2.120", {"start": v(25.64, 34.47) * mm, "end": v(25.64, 36.2) * mm});
            skLineSegment(sketch, "E51.0.2.121", {"start": v(10.21, 36.2) * mm, "end": v(10.21, 34.47) * mm});
            skLineSegment(sketch, "E51.0.2.122", {"start": v(31.71, 30.88) * mm, "end": v(31.71, 29.15) * mm});
            skLineSegment(sketch, "E51.0.2.123", {"start": v(24.07, 31.74) * mm, "end": v(25.57, 30.88) * mm});
            skLineSegment(sketch, "E51.0.2.124", {"start": v(13.29, 29.15) * mm, "end": v(11.79, 28.28) * mm});
            skLineSegment(sketch, "E51.0.2.125", {"start": v(33.29, 37.06) * mm, "end": v(34.79, 36.2) * mm});
            skLineSegment(sketch, "E51.0.3.0", {"start": v(37.86, 41.52) * mm, "end": v(41, 41.52) * mm});
            skCircle(sketch, "E51.0.3.1", {"center": v(-0.5, 40.65) * mm, "radius": 1.5 * mm, "construction": true});
            skCircle(sketch, "E51.0.3.2", {"center": v(24.07, 40.65) * mm, "radius": 1.5 * mm, "construction": true});
            skLineSegment(sketch, "E51.0.3.3", {"start": v(10.29, 39.79) * mm, "end": v(10.29, 41.52) * mm});
            skCircle(sketch, "E51.0.3.4", {"center": v(11.79, 40.65) * mm, "radius": 1.5 * mm, "construction": true});
            skPoint(sketch, "E51.0.3.5", {"position": v(2.57, 41.52) * mm});
            skCircle(sketch, "E51.0.3.6", {"center": v(17.93, 40.65) * mm, "radius": 1.5 * mm, "construction": true});
            skLineSegment(sketch, "E51.0.3.7", {"start": v(30.21, 38.92) * mm, "end": v(28.71, 39.79) * mm});
            skLineSegment(sketch, "E51.0.3.8", {"start": v(1.07, 45.1) * mm, "end": v(7.21, 45.1) * mm, "construction": true});
            skLineSegment(sketch, "E51.0.3.9", {"start": v(13.36, 46.84) * mm, "end": v(14.86, 47.7) * mm});
            skPoint(sketch, "E51.0.3.10", {"position": v(21.75, 47.27) * mm});
            skPoint(sketch, "E51.0.3.11", {"position": v(43.25, 41.95) * mm});
            skLineSegment(sketch, "E51.0.3.12", {"start": v(7.21, 46.84) * mm, "end": v(8.71, 47.7) * mm});
            skLineSegment(sketch, "E51.0.3.13", {"start": v(2.57, 44.24) * mm, "end": v(1.07, 45.1) * mm});
            skCircle(sketch, "E51.0.3.14", {"center": v(39.43, 45.97) * mm, "radius": 1.5 * mm, "construction": true});
            skLineSegment(sketch, "E51.0.3.15", {"start": v(10.29, 41.52) * mm, "end": v(11.79, 42.38) * mm});
            skLineSegment(sketch, "E51.0.3.16", {"start": v(37.86, 39.79) * mm, "end": v(36.36, 38.92) * mm});
            skLineSegment(sketch, "E51.0.3.17", {"start": v(44, 39.79) * mm, "end": v(42.5, 38.92) * mm});
            skCircle(sketch, "E51.0.3.18", {"center": v(36.36, 40.65) * mm, "radius": 1.5 * mm, "construction": true});
            skPoint(sketch, "E51.0.3.19", {"position": v(18.68, 41.95) * mm});
            skPoint(sketch, "E51.0.3.20", {"position": v(40.18, 47.27) * mm});
            skLineSegment(sketch, "E51.0.3.21", {"start": v(28.71, 41.52) * mm, "end": v(30.21, 42.38) * mm});
            skCircle(sketch, "E51.0.3.22", {"center": v(2.57, 45.97) * mm, "radius": 1.5 * mm, "construction": true});
            skLineSegment(sketch, "E51.0.3.23", {"start": v(13.36, 45.1) * mm, "end": v(13.36, 46.84) * mm});
            skPoint(sketch, "E51.0.3.24", {"position": v(15.6, 47.27) * mm});
            skPoint(sketch, "E51.0.3.25", {"position": v(37.1, 41.95) * mm});
            skLineSegment(sketch, "E51.0.3.26", {"start": v(13.29, 41.52) * mm, "end": v(13.29, 39.79) * mm});
            skLineSegment(sketch, "E51.0.3.27", {"start": v(41, 39.79) * mm, "end": v(41, 41.52) * mm});
            skLineSegment(sketch, "E51.0.3.28", {"start": v(1, 39.79) * mm, "end": v(-0.5, 38.92) * mm});
            skLineSegment(sketch, "E51.0.3.29", {"start": v(36.36, 38.92) * mm, "end": v(34.86, 39.79) * mm});
            skLineSegment(sketch, "E51.0.3.30", {"start": v(4.07, 45.1) * mm, "end": v(2.57, 44.24) * mm});
            skPoint(sketch, "E51.0.3.31", {"position": v(24.82, 41.95) * mm});
            skLineSegment(sketch, "E51.0.3.32", {"start": v(16.36, 46.84) * mm, "end": v(16.36, 45.1) * mm});
            skLineSegment(sketch, "E51.0.3.33", {"start": v(22.5, 46.84) * mm, "end": v(22.5, 45.1) * mm});
            skLineSegment(sketch, "E51.0.3.34", {"start": v(37.93, 45.1) * mm, "end": v(37.93, 46.84) * mm});
            skLineSegment(sketch, "E51.0.3.35", {"start": v(44, 41.52) * mm, "end": v(44, 39.79) * mm});
            skPoint(sketch, "E51.0.3.36", {"position": v(0.25, 41.95) * mm});
            skPoint(sketch, "E51.0.3.37", {"position": v(3.32, 47.27) * mm});
            skPoint(sketch, "E51.0.3.38", {"position": v(39.43, 41.52) * mm});
            skLineSegment(sketch, "E51.0.3.39", {"start": v(14.86, 44.24) * mm, "end": v(13.36, 45.1) * mm});
            skCircle(sketch, "E51.0.3.40", {"center": v(33.29, 45.97) * mm, "radius": 1.5 * mm, "construction": true});
            skLineSegment(sketch, "E51.0.3.41", {"start": v(10.21, 45.1) * mm, "end": v(8.71, 44.24) * mm});
            skCircle(sketch, "E51.0.3.42", {"center": v(30.21, 40.65) * mm, "radius": 1.5 * mm, "construction": true});
            skLineSegment(sketch, "E51.0.3.43", {"start": v(42.5, 38.92) * mm, "end": v(41, 39.79) * mm});
            skLineSegment(sketch, "E51.0.3.44", {"start": v(25.64, 46.84) * mm, "end": v(27.14, 47.7) * mm});
            skLineSegment(sketch, "E51.0.3.45", {"start": v(19.43, 41.52) * mm, "end": v(19.43, 39.79) * mm});
            skLineSegment(sketch, "E51.0.3.46", {"start": v(-2, 39.79) * mm, "end": v(4.14, 39.79) * mm, "construction": true});
            skCircle(sketch, "E51.0.3.47", {"center": v(14.86, 45.97) * mm, "radius": 1.5 * mm, "construction": true});
            skLineSegment(sketch, "E51.0.3.48", {"start": v(19.43, 39.79) * mm, "end": v(17.93, 38.92) * mm});
            skLineSegment(sketch, "E51.0.3.49", {"start": v(-0.5, 38.92) * mm, "end": v(-2, 39.79) * mm});
            skLineSegment(sketch, "E51.0.3.50", {"start": v(-2, 41.52) * mm, "end": v(-0.5, 42.38) * mm});
            skLineSegment(sketch, "E51.0.3.51", {"start": v(31.71, 39.79) * mm, "end": v(30.21, 38.92) * mm});
            skLineSegment(sketch, "E51.0.3.52", {"start": v(25.57, 39.79) * mm, "end": v(24.07, 38.92) * mm});
            skLineSegment(sketch, "E51.0.3.53", {"start": v(16.43, 39.79) * mm, "end": v(16.43, 41.52) * mm});
            skLineSegment(sketch, "E51.0.3.54", {"start": v(40.93, 45.1) * mm, "end": v(39.43, 44.24) * mm});
            skCircle(sketch, "E51.0.3.55", {"center": v(27.14, 45.97) * mm, "radius": 1.5 * mm, "construction": true});
            skCircle(sketch, "E51.0.3.56", {"center": v(21, 45.97) * mm, "radius": 1.5 * mm, "construction": true});
            skLineSegment(sketch, "E51.0.3.57", {"start": v(8.71, 44.24) * mm, "end": v(7.21, 45.1) * mm});
            skLineSegment(sketch, "E51.0.3.58", {"start": v(1.07, 46.84) * mm, "end": v(2.57, 47.7) * mm});
            skCircle(sketch, "E51.0.3.59", {"center": v(5.64, 40.65) * mm, "radius": 1.5 * mm, "construction": true});
            skLineSegment(sketch, "E51.0.3.60", {"start": v(5.64, 38.92) * mm, "end": v(4.14, 39.79) * mm});
            skLineSegment(sketch, "E51.0.3.61", {"start": v(7.14, 39.79) * mm, "end": v(5.64, 38.92) * mm});
            skPoint(sketch, "E51.0.3.62", {"position": v(27.9, 47.27) * mm});
            skPoint(sketch, "E51.0.3.63", {"position": v(6.4, 41.95) * mm});
            skPoint(sketch, "E51.0.3.64", {"position": v(9.46, 47.27) * mm});
            skLineSegment(sketch, "E51.0.3.65", {"start": v(11.79, 38.92) * mm, "end": v(10.29, 39.79) * mm});
            skLineSegment(sketch, "E51.0.3.66", {"start": v(31.79, 46.84) * mm, "end": v(33.29, 47.7) * mm});
            skLineSegment(sketch, "E51.0.3.67", {"start": v(19.5, 45.1) * mm, "end": v(19.5, 46.84) * mm});
            skLineSegment(sketch, "E51.0.3.68", {"start": v(1, 41.52) * mm, "end": v(4.14, 41.52) * mm});
            skPoint(sketch, "E51.0.3.69", {"position": v(30.96, 41.95) * mm});
            skLineSegment(sketch, "E51.0.3.70", {"start": v(17.93, 38.92) * mm, "end": v(16.43, 39.79) * mm});
            skLineSegment(sketch, "E51.0.3.71", {"start": v(41, 41.52) * mm, "end": v(42.5, 42.38) * mm});
            skLineSegment(sketch, "E51.0.3.72", {"start": v(37.93, 46.84) * mm, "end": v(39.43, 47.7) * mm});
            skPoint(sketch, "E51.0.3.73", {"position": v(12.54, 41.95) * mm});
            skCircle(sketch, "E51.0.3.74", {"center": v(42.5, 40.65) * mm, "radius": 1.5 * mm, "construction": true});
            skLineSegment(sketch, "E51.0.3.75", {"start": v(22.5, 45.1) * mm, "end": v(21, 44.24) * mm});
            skCircle(sketch, "E51.0.3.76", {"center": v(8.71, 45.97) * mm, "radius": 1.5 * mm, "construction": true});
            skPoint(sketch, "E51.0.3.77", {"position": v(34.04, 47.27) * mm});
            skLineSegment(sketch, "E51.0.3.78", {"start": v(4.14, 41.52) * mm, "end": v(5.64, 42.38) * mm});
            skLineSegment(sketch, "E51.0.3.79", {"start": v(21, 44.24) * mm, "end": v(19.5, 45.1) * mm});
            skLineSegment(sketch, "E51.0.3.80", {"start": v(22.57, 39.79) * mm, "end": v(22.57, 41.52) * mm});
            skLineSegment(sketch, "E51.0.3.81", {"start": v(28.71, 39.79) * mm, "end": v(28.71, 41.52) * mm});
            skLineSegment(sketch, "E51.0.3.82", {"start": v(16.36, 45.1) * mm, "end": v(14.86, 44.24) * mm});
            skLineSegment(sketch, "E51.0.3.83", {"start": v(27.14, 47.7) * mm, "end": v(28.64, 46.84) * mm});
            skLineSegment(sketch, "E51.0.3.84", {"start": v(21, 47.7) * mm, "end": v(22.5, 46.84) * mm});
            skLineSegment(sketch, "E51.0.3.85", {"start": v(11.79, 42.38) * mm, "end": v(13.29, 41.52) * mm});
            skLineSegment(sketch, "E51.0.3.86", {"start": v(7.21, 45.1) * mm, "end": v(7.21, 46.84) * mm});
            skLineSegment(sketch, "E51.0.3.87", {"start": v(19.5, 46.84) * mm, "end": v(21, 47.7) * mm});
            skLineSegment(sketch, "E51.0.3.88", {"start": v(33.29, 44.24) * mm, "end": v(31.79, 45.1) * mm});
            skLineSegment(sketch, "E51.0.3.89", {"start": v(1, 41.52) * mm, "end": v(1, 39.79) * mm});
            skLineSegment(sketch, "E51.0.3.90", {"start": v(-0.5, 42.38) * mm, "end": v(1, 41.52) * mm});
            skLineSegment(sketch, "E51.0.3.91", {"start": v(14.86, 47.7) * mm, "end": v(16.36, 46.84) * mm});
            skLineSegment(sketch, "E51.0.3.92", {"start": v(28.64, 46.84) * mm, "end": v(28.64, 45.1) * mm});
            skLineSegment(sketch, "E51.0.3.93", {"start": v(1.07, 45.1) * mm, "end": v(1.07, 46.84) * mm});
            skLineSegment(sketch, "E51.0.3.94", {"start": v(8.71, 47.7) * mm, "end": v(10.21, 46.84) * mm});
            skLineSegment(sketch, "E51.0.3.95", {"start": v(31.79, 45.1) * mm, "end": v(31.79, 46.84) * mm});
            skLineSegment(sketch, "E51.0.3.96", {"start": v(24.07, 38.92) * mm, "end": v(22.57, 39.79) * mm});
            skLineSegment(sketch, "E51.0.3.97", {"start": v(37.86, 41.52) * mm, "end": v(37.86, 39.79) * mm});
            skLineSegment(sketch, "E51.0.3.98", {"start": v(34.86, 39.79) * mm, "end": v(34.86, 41.52) * mm});
            skLineSegment(sketch, "E51.0.3.99", {"start": v(4.07, 46.84) * mm, "end": v(4.07, 45.1) * mm});
            skLineSegment(sketch, "E51.0.3.100", {"start": v(27.14, 44.24) * mm, "end": v(25.64, 45.1) * mm});
            skLineSegment(sketch, "E51.0.3.101", {"start": v(16.43, 41.52) * mm, "end": v(17.93, 42.38) * mm});
            skLineSegment(sketch, "E51.0.3.102", {"start": v(40.93, 46.84) * mm, "end": v(40.93, 45.1) * mm});
            skLineSegment(sketch, "E51.0.3.103", {"start": v(2.57, 47.7) * mm, "end": v(4.07, 46.84) * mm});
            skLineSegment(sketch, "E51.0.3.104", {"start": v(17.93, 42.38) * mm, "end": v(19.43, 41.52) * mm});
            skLineSegment(sketch, "E51.0.3.105", {"start": v(34.79, 46.84) * mm, "end": v(34.79, 45.1) * mm});
            skLineSegment(sketch, "E51.0.3.106", {"start": v(39.43, 44.24) * mm, "end": v(37.93, 45.1) * mm});
            skLineSegment(sketch, "E51.0.3.107", {"start": v(22.57, 41.52) * mm, "end": v(24.07, 42.38) * mm});
            skLineSegment(sketch, "E51.0.3.108", {"start": v(39.43, 47.7) * mm, "end": v(40.93, 46.84) * mm});
            skLineSegment(sketch, "E51.0.3.109", {"start": v(30.21, 42.38) * mm, "end": v(31.71, 41.52) * mm});
            skLineSegment(sketch, "E51.0.3.110", {"start": v(28.64, 45.1) * mm, "end": v(27.14, 44.24) * mm});
            skLineSegment(sketch, "E51.0.3.111", {"start": v(-2, 39.79) * mm, "end": v(-2, 41.52) * mm});
            skLineSegment(sketch, "E51.0.3.112", {"start": v(42.5, 42.38) * mm, "end": v(44, 41.52) * mm});
            skLineSegment(sketch, "E51.0.3.113", {"start": v(36.36, 42.38) * mm, "end": v(37.86, 41.52) * mm});
            skLineSegment(sketch, "E51.0.3.114", {"start": v(34.79, 45.1) * mm, "end": v(33.29, 44.24) * mm});
            skLineSegment(sketch, "E51.0.3.115", {"start": v(4.14, 39.79) * mm, "end": v(4.14, 41.52) * mm});
            skLineSegment(sketch, "E51.0.3.116", {"start": v(7.14, 41.52) * mm, "end": v(7.14, 39.79) * mm});
            skLineSegment(sketch, "E51.0.3.117", {"start": v(5.64, 42.38) * mm, "end": v(7.14, 41.52) * mm});
            skLineSegment(sketch, "E51.0.3.118", {"start": v(34.86, 41.52) * mm, "end": v(36.36, 42.38) * mm});
            skLineSegment(sketch, "E51.0.3.119", {"start": v(25.57, 41.52) * mm, "end": v(25.57, 39.79) * mm});
            skLineSegment(sketch, "E51.0.3.120", {"start": v(25.64, 45.1) * mm, "end": v(25.64, 46.84) * mm});
            skLineSegment(sketch, "E51.0.3.121", {"start": v(10.21, 46.84) * mm, "end": v(10.21, 45.1) * mm});
            skLineSegment(sketch, "E51.0.3.122", {"start": v(31.71, 41.52) * mm, "end": v(31.71, 39.79) * mm});
            skLineSegment(sketch, "E51.0.3.123", {"start": v(24.07, 42.38) * mm, "end": v(25.57, 41.52) * mm});
            skLineSegment(sketch, "E51.0.3.124", {"start": v(13.29, 39.79) * mm, "end": v(11.79, 38.92) * mm});
            skLineSegment(sketch, "E51.0.3.125", {"start": v(33.29, 47.7) * mm, "end": v(34.79, 46.84) * mm});
            skLineSegment(sketch, "E51.direction1", {"start": v(-2, 7.87) * mm, "end": v(7.1, 7.87) * mm, "construction": true});
            skLineSegment(sketch, "E51.direction2", {"start": v(-2, 7.87) * mm, "end": v(-2, 18.5) * mm, "construction": true});
            skSolve(sketch);
        }
        {
            var Q0;
            Q0=makeQuery(id+"F13.imprint","IMPRINT",FACE,{"disambiguationData":[TD([[makeQuery(id+"F13.imprint","IMPRINT",EDGE,{"derivedFrom":sQuery(id+"F13.wireOp",EDGE,"E51.0.2.45")}),-1.0]])]});
            var Q1;
            Q1=makeQuery(id+"F13.imprint","IMPRINT",FACE,{"disambiguationData":[TD([[makeQuery(id+"F13.imprint","IMPRINT",EDGE,{"derivedFrom":sQuery(id+"F13.wireOp",EDGE,"E51.0.2.52")}),-1.0]])]});
            var Q2;
            Q2=makeQuery(id+"F13.imprint","IMPRINT",FACE,{"disambiguationData":[TD([[makeQuery(id+"F13.imprint","IMPRINT",EDGE,{"derivedFrom":sQuery(id+"F13.wireOp",EDGE,"E51.0.2.60")}),-1.0]])]});
            var Q3;
            Q3=makeQuery(id+"F13.imprint","IMPRINT",FACE,{"disambiguationData":[TD([[makeQuery(id+"F13.imprint","IMPRINT",EDGE,{"derivedFrom":sQuery(id+"F13.wireOp",EDGE,"E51.0.2.66")}),-1.0]])]});
            var Q4;
            Q4=makeQuery(id+"F13.imprint","IMPRINT",FACE,{"disambiguationData":[TD([[makeQuery(id+"F13.imprint","IMPRINT",EDGE,{"derivedFrom":sQuery(id+"F13.wireOp",EDGE,"E51.0.2.7")}),-1.0]])]});
            var Q5;
            Q5=makeQuery(id+"F13.imprint","IMPRINT",FACE,{"disambiguationData":[TD([[makeQuery(id+"F13.imprint","IMPRINT",EDGE,{"derivedFrom":sQuery(id+"F13.wireOp",EDGE,"E51.0.2.3")}),-1.0]])]});
            var Q6;
            Q6=makeQuery(id+"F13.imprint","IMPRINT",FACE,{"disambiguationData":[TD([[makeQuery(id+"F13.imprint","IMPRINT",EDGE,{"derivedFrom":sQuery(id+"F13.wireOp",EDGE,"E51.0.2.12")}),-1.0]])]});
            var Q7;
            Q7=makeQuery(id+"F13.imprint","IMPRINT",FACE,{"disambiguationData":[TD([[makeQuery(id+"F13.imprint","IMPRINT",EDGE,{"derivedFrom":sQuery(id+"F13.wireOp",EDGE,"E51.0.2.16")}),-1.0]])]});
            var Q8;
            Q8=makeQuery(id+"F13.imprint","IMPRINT",FACE,{"disambiguationData":[TD([[makeQuery(id+"F13.imprint","IMPRINT",EDGE,{"derivedFrom":sQuery(id+"F13.wireOp",EDGE,"E51.0.2.17")}),-1.0]])]});
            var Q9;
            Q9=makeQuery(id+"F13.imprint","IMPRINT",FACE,{"disambiguationData":[TD([[makeQuery(id+"F13.imprint","IMPRINT",EDGE,{"derivedFrom":sQuery(id+"F13.wireOp",EDGE,"E51.0.2.28")}),-1.0]])]});
            var Q10;
            Q10=makeQuery(id+"F13.imprint","IMPRINT",FACE,{"disambiguationData":[TD([[makeQuery(id+"F13.imprint","IMPRINT",EDGE,{"derivedFrom":sQuery(id+"F13.wireOp",EDGE,"E51.0.1.45")}),-1.0]])]});
            var Q11;
            Q11=makeQuery(id+"F13.imprint","IMPRINT",FACE,{"disambiguationData":[TD([[makeQuery(id+"F13.imprint","IMPRINT",EDGE,{"derivedFrom":sQuery(id+"F13.wireOp",EDGE,"E51.0.3.52")}),-1.0]])]});
            var Q12;
            Q12=makeQuery(id+"F13.imprint","IMPRINT",FACE,{"disambiguationData":[TD([[makeQuery(id+"F13.imprint","IMPRINT",EDGE,{"derivedFrom":sQuery(id+"F13.wireOp",EDGE,"E51.0.1.44")}),-1.0]])]});
            var Q13;
            Q13=makeQuery(id+"F13.imprint","IMPRINT",FACE,{"disambiguationData":[TD([[makeQuery(id+"F13.imprint","IMPRINT",EDGE,{"derivedFrom":sQuery(id+"F13.wireOp",EDGE,"E51.0.3.66")}),-1.0]])]});
            var Q14;
            Q14=makeQuery(id+"F13.imprint","IMPRINT",FACE,{"disambiguationData":[TD([[makeQuery(id+"F13.imprint","IMPRINT",EDGE,{"derivedFrom":sQuery(id+"F13.wireOp",EDGE,"E51.0.1.52")}),-1.0]])]});
            var Q15;
            Q15=makeQuery(id+"F13.imprint","IMPRINT",FACE,{"disambiguationData":[TD([[makeQuery(id+"F13.imprint","IMPRINT",EDGE,{"derivedFrom":sQuery(id+"F13.wireOp",EDGE,"E51.0.3.60")}),-1.0]])]});
            var Q16;
            Q16=makeQuery(id+"F13.imprint","IMPRINT",FACE,{"disambiguationData":[TD([[makeQuery(id+"F13.imprint","IMPRINT",EDGE,{"derivedFrom":sQuery(id+"F13.wireOp",EDGE,"E48.4.0.1")}),-1.0]])]});
            var Q17;
            Q17=makeQuery(id+"F13.imprint","IMPRINT",FACE,{"disambiguationData":[TD([[makeQuery(id+"F13.imprint","IMPRINT",EDGE,{"derivedFrom":sQuery(id+"F13.wireOp",EDGE,"E51.0.1.60")}),-1.0]])]});
            var Q18;
            Q18=makeQuery(id+"F13.imprint","IMPRINT",FACE,{"disambiguationData":[TD([[makeQuery(id+"F13.imprint","IMPRINT",EDGE,{"derivedFrom":sQuery(id+"F13.wireOp",EDGE,"E48.5.0.1")}),-1.0]])]});
            var Q19;
            Q19=makeQuery(id+"F13.imprint","IMPRINT",FACE,{"disambiguationData":[TD([[makeQuery(id+"F13.imprint","IMPRINT",EDGE,{"derivedFrom":sQuery(id+"F13.wireOp",EDGE,"E51.0.1.3")}),-1.0]])]});
            var Q20;
            Q20=makeQuery(id+"F13.imprint","IMPRINT",FACE,{"disambiguationData":[TD([[makeQuery(id+"F13.imprint","IMPRINT",EDGE,{"derivedFrom":sQuery(id+"F13.wireOp",EDGE,"E43.0")}),-1.0]])]});
            var Q21;
            Q21=makeQuery(id+"F13.imprint","IMPRINT",FACE,{"disambiguationData":[TD([[makeQuery(id+"F13.imprint","IMPRINT",EDGE,{"derivedFrom":sQuery(id+"F13.wireOp",EDGE,"E44.1.0.2")}),-1.0]])]});
            var Q22;
            Q22=makeQuery(id+"F13.imprint","IMPRINT",FACE,{"disambiguationData":[TD([[makeQuery(id+"F13.imprint","IMPRINT",EDGE,{"derivedFrom":sQuery(id+"F13.wireOp",EDGE,"E44.4.0.2")}),-1.0]])]});
            var Q23;
            Q23=makeQuery(id+"F13.imprint","IMPRINT",FACE,{"disambiguationData":[TD([[makeQuery(id+"F13.imprint","IMPRINT",EDGE,{"derivedFrom":sQuery(id+"F13.wireOp",EDGE,"E45.0")}),-1.0]])]});
            var Q24;
            Q24=makeQuery(id+"F13.imprint","IMPRINT",FACE,{"disambiguationData":[TD([[makeQuery(id+"F13.imprint","IMPRINT",EDGE,{"derivedFrom":sQuery(id+"F13.wireOp",EDGE,"E44.7.0.2")}),-1.0]])]});
            var Q25;
            Q25=makeQuery(id+"F13.imprint","IMPRINT",FACE,{"disambiguationData":[TD([[makeQuery(id+"F13.imprint","IMPRINT",EDGE,{"derivedFrom":sQuery(id+"F13.wireOp",EDGE,"E44.6.0.2")}),-1.0]])]});
            var Q26;
            Q26=makeQuery(id+"F13.imprint","IMPRINT",FACE,{"disambiguationData":[TD([[makeQuery(id+"F13.imprint","IMPRINT",EDGE,{"derivedFrom":sQuery(id+"F13.wireOp",EDGE,"E48.6.0.1")}),-1.0]])]});
            var Q27;
            Q27=makeQuery(id+"F13.imprint","IMPRINT",FACE,{"disambiguationData":[TD([[makeQuery(id+"F13.imprint","IMPRINT",EDGE,{"derivedFrom":sQuery(id+"F13.wireOp",EDGE,"E44.2.0.2")}),-1.0]])]});
            var Q28;
            Q28=makeQuery(id+"F13.imprint","IMPRINT",FACE,{"disambiguationData":[TD([[makeQuery(id+"F13.imprint","IMPRINT",EDGE,{"derivedFrom":sQuery(id+"F13.wireOp",EDGE,"E44.3.0.2")}),-1.0]])]});
            var Q29;
            Q29=makeQuery(id+"F13.imprint","IMPRINT",FACE,{"disambiguationData":[TD([[makeQuery(id+"F13.imprint","IMPRINT",EDGE,{"derivedFrom":sQuery(id+"F13.wireOp",EDGE,"E48.2.0.1")}),-1.0]])]});
            var Q30;
            Q30=makeQuery(id+"F13.imprint","IMPRINT",FACE,{"disambiguationData":[TD([[makeQuery(id+"F13.imprint","IMPRINT",EDGE,{"derivedFrom":sQuery(id+"F13.wireOp",EDGE,"E48.3.0.1")}),-1.0]])]});
            var Q31;
            Q31=makeQuery(id+"F13.imprint","IMPRINT",FACE,{"disambiguationData":[TD([[makeQuery(id+"F13.imprint","IMPRINT",EDGE,{"derivedFrom":sQuery(id+"F13.wireOp",EDGE,"E48.1.0.1")}),-1.0]])]});
            var Q32;
            Q32=makeQuery(id+"F13.imprint","IMPRINT",FACE,{"disambiguationData":[TD([[makeQuery(id+"F13.imprint","IMPRINT",EDGE,{"derivedFrom":sQuery(id+"F13.wireOp",EDGE,"E44.5.0.2")}),-1.0]])]});
            var Q33;
            Q33=makeQuery(id+"F13.imprint","IMPRINT",FACE,{"disambiguationData":[TD([[makeQuery(id+"F13.imprint","IMPRINT",EDGE,{"derivedFrom":sQuery(id+"F13.wireOp",EDGE,"E51.0.3.9")}),-1.0]])]});
            var Q34;
            Q34=makeQuery(id+"F13.imprint","IMPRINT",FACE,{"disambiguationData":[TD([[makeQuery(id+"F13.imprint","IMPRINT",EDGE,{"derivedFrom":sQuery(id+"F13.wireOp",EDGE,"E51.0.1.66")}),-1.0]])]});
            var Q35;
            Q35=makeQuery(id+"F13.imprint","IMPRINT",FACE,{"disambiguationData":[TD([[makeQuery(id+"F13.imprint","IMPRINT",EDGE,{"derivedFrom":sQuery(id+"F13.wireOp",EDGE,"E51.0.3.3")}),-1.0]])]});
            var Q36;
            Q36=makeQuery(id+"F13.imprint","IMPRINT",FACE,{"disambiguationData":[TD([[makeQuery(id+"F13.imprint","IMPRINT",EDGE,{"derivedFrom":sQuery(id+"F13.wireOp",EDGE,"E51.0.3.7")}),-1.0]])]});
            var Q37;
            Q37=makeQuery(id+"F13.imprint","IMPRINT",FACE,{"disambiguationData":[TD([[makeQuery(id+"F13.imprint","IMPRINT",EDGE,{"derivedFrom":sQuery(id+"F13.wireOp",EDGE,"E51.0.3.12")}),-1.0]])]});
            var Q38;
            Q38=makeQuery(id+"F13.imprint","IMPRINT",FACE,{"disambiguationData":[TD([[makeQuery(id+"F13.imprint","IMPRINT",EDGE,{"derivedFrom":sQuery(id+"F13.wireOp",EDGE,"E51.0.2.9")}),-1.0]])]});
            var Q39;
            Q39=makeQuery(id+"F13.imprint","IMPRINT",FACE,{"disambiguationData":[TD([[makeQuery(id+"F13.imprint","IMPRINT",EDGE,{"derivedFrom":sQuery(id+"F13.wireOp",EDGE,"E51.0.1.7")}),-1.0]])]});
            var Q40;
            Q40=makeQuery(id+"F13.imprint","IMPRINT",FACE,{"disambiguationData":[TD([[makeQuery(id+"F13.imprint","IMPRINT",EDGE,{"derivedFrom":sQuery(id+"F13.wireOp",EDGE,"E51.0.3.13")}),-1.0]])]});
            var Q41;
            Q41=makeQuery(id+"F13.imprint","IMPRINT",FACE,{"disambiguationData":[TD([[makeQuery(id+"F13.imprint","IMPRINT",EDGE,{"derivedFrom":sQuery(id+"F13.wireOp",EDGE,"E51.0.1.9")}),-1.0]])]});
            var Q42;
            Q42=makeQuery(id+"F13.imprint","IMPRINT",FACE,{"disambiguationData":[TD([[makeQuery(id+"F13.imprint","IMPRINT",EDGE,{"derivedFrom":sQuery(id+"F13.wireOp",EDGE,"E51.0.2.13")}),-1.0]])]});
            var Q43;
            Q43=makeQuery(id+"F13.imprint","IMPRINT",FACE,{"disambiguationData":[TD([[makeQuery(id+"F13.imprint","IMPRINT",EDGE,{"derivedFrom":sQuery(id+"F13.wireOp",EDGE,"E51.0.3.16")}),-1.0]])]});
            var Q44;
            Q44=makeQuery(id+"F13.imprint","IMPRINT",FACE,{"disambiguationData":[TD([[makeQuery(id+"F13.imprint","IMPRINT",EDGE,{"derivedFrom":sQuery(id+"F13.wireOp",EDGE,"E51.0.1.12")}),-1.0]])]});
            var Q45;
            Q45=makeQuery(id+"F13.imprint","IMPRINT",FACE,{"disambiguationData":[TD([[makeQuery(id+"F13.imprint","IMPRINT",EDGE,{"derivedFrom":sQuery(id+"F13.wireOp",EDGE,"E51.0.3.17")}),-1.0]])]});
            var Q46;
            Q46=makeQuery(id+"F13.imprint","IMPRINT",FACE,{"disambiguationData":[TD([[makeQuery(id+"F13.imprint","IMPRINT",EDGE,{"derivedFrom":sQuery(id+"F13.wireOp",EDGE,"E51.0.1.13")}),-1.0]])]});
            var Q47;
            Q47=makeQuery(id+"F13.imprint","IMPRINT",FACE,{"disambiguationData":[TD([[makeQuery(id+"F13.imprint","IMPRINT",EDGE,{"derivedFrom":sQuery(id+"F13.wireOp",EDGE,"E51.0.3.28")}),-1.0]])]});
            var Q48;
            Q48=makeQuery(id+"F13.imprint","IMPRINT",FACE,{"disambiguationData":[TD([[makeQuery(id+"F13.imprint","IMPRINT",EDGE,{"derivedFrom":sQuery(id+"F13.wireOp",EDGE,"E51.0.1.16")}),-1.0]])]});
            var Q49;
            Q49=makeQuery(id+"F13.imprint","IMPRINT",FACE,{"disambiguationData":[TD([[makeQuery(id+"F13.imprint","IMPRINT",EDGE,{"derivedFrom":sQuery(id+"F13.wireOp",EDGE,"E51.0.3.33")}),-1.0]])]});
            var Q50;
            Q50=makeQuery(id+"F13.imprint","IMPRINT",FACE,{"disambiguationData":[TD([[makeQuery(id+"F13.imprint","IMPRINT",EDGE,{"derivedFrom":sQuery(id+"F13.wireOp",EDGE,"E51.0.1.17")}),-1.0]])]});
            var Q51;
            Q51=makeQuery(id+"F13.imprint","IMPRINT",FACE,{"disambiguationData":[TD([[makeQuery(id+"F13.imprint","IMPRINT",EDGE,{"derivedFrom":sQuery(id+"F13.wireOp",EDGE,"E51.0.1.34")}),-1.0]])]});
            var Q52;
            Q52=makeQuery(id+"F13.imprint","IMPRINT",FACE,{"disambiguationData":[TD([[makeQuery(id+"F13.imprint","IMPRINT",EDGE,{"derivedFrom":sQuery(id+"F13.wireOp",EDGE,"E51.0.3.44")}),-1.0]])]});
            var Q53;
            Q53=makeQuery(id+"F13.imprint","IMPRINT",FACE,{"disambiguationData":[TD([[makeQuery(id+"F13.imprint","IMPRINT",EDGE,{"derivedFrom":sQuery(id+"F13.wireOp",EDGE,"E51.0.2.33")}),-1.0]])]});
            var Q54;
            Q54=makeQuery(id+"F13.imprint","IMPRINT",FACE,{"disambiguationData":[TD([[makeQuery(id+"F13.imprint","IMPRINT",EDGE,{"derivedFrom":sQuery(id+"F13.wireOp",EDGE,"E51.0.1.28")}),-1.0]])]});
            var Q55;
            Q55=makeQuery(id+"F13.imprint","IMPRINT",FACE,{"disambiguationData":[TD([[makeQuery(id+"F13.imprint","IMPRINT",EDGE,{"derivedFrom":sQuery(id+"F13.wireOp",EDGE,"E51.0.2.34")}),-1.0]])]});
            var Q56;
            Q56=makeQuery(id+"F13.imprint","IMPRINT",FACE,{"disambiguationData":[TD([[makeQuery(id+"F13.imprint","IMPRINT",EDGE,{"derivedFrom":sQuery(id+"F13.wireOp",EDGE,"E51.0.1.33")}),-1.0]])]});
            var Q57;
            Q57=makeQuery(id+"F13.imprint","IMPRINT",FACE,{"disambiguationData":[TD([[makeQuery(id+"F13.imprint","IMPRINT",EDGE,{"derivedFrom":sQuery(id+"F13.wireOp",EDGE,"E51.0.3.34")}),-1.0]])]});
            var Q58;
            Q58=makeQuery(id+"F13.imprint","IMPRINT",FACE,{"disambiguationData":[TD([[makeQuery(id+"F13.imprint","IMPRINT",EDGE,{"derivedFrom":sQuery(id+"F13.wireOp",EDGE,"E51.0.2.44")}),-1.0]])]});
            var Q59;
            Q59=makeQuery(id+"F13.imprint","IMPRINT",FACE,{"disambiguationData":[TD([[makeQuery(id+"F13.imprint","IMPRINT",EDGE,{"derivedFrom":sQuery(id+"F13.wireOp",EDGE,"E51.0.3.45")}),-1.0]])]});
            var Q60;
            Q60=makeQuery(id+"F3.opExtrude","SWEPT_FACE",FACE,{"disambiguationData":[OSD([sQuery(id+"F2.wireOp",EDGE,"E14.top")])]});
            extrude(context, id + "F14", {"entities" : qUnion([Q0, Q1, Q2, Q3, Q4, Q5, Q6, Q7, Q8, Q9, Q10, Q11, Q12, Q13, Q14, Q15, Q16, Q17, Q18, Q19, Q20, Q21, Q22, Q23, Q24, Q25, Q26, Q27, Q28, Q29, Q30, Q31, Q32, Q33, Q34, Q35, Q36, Q37, Q38, Q39, Q40, Q41, Q42, Q43, Q44, Q45, Q46, Q47, Q48, Q49, Q50, Q51, Q52, Q53, Q54, Q55, Q56, Q57, Q58, Q59]), "operationType" : NewBodyOperationType.REMOVE, "endBound" : BoundingType.UP_TO_SURFACE, "oppositeDirection" : true, "endBoundEntityFace" : qUnion([Q60]), "depth" : 25 * mm});
        }
    });
